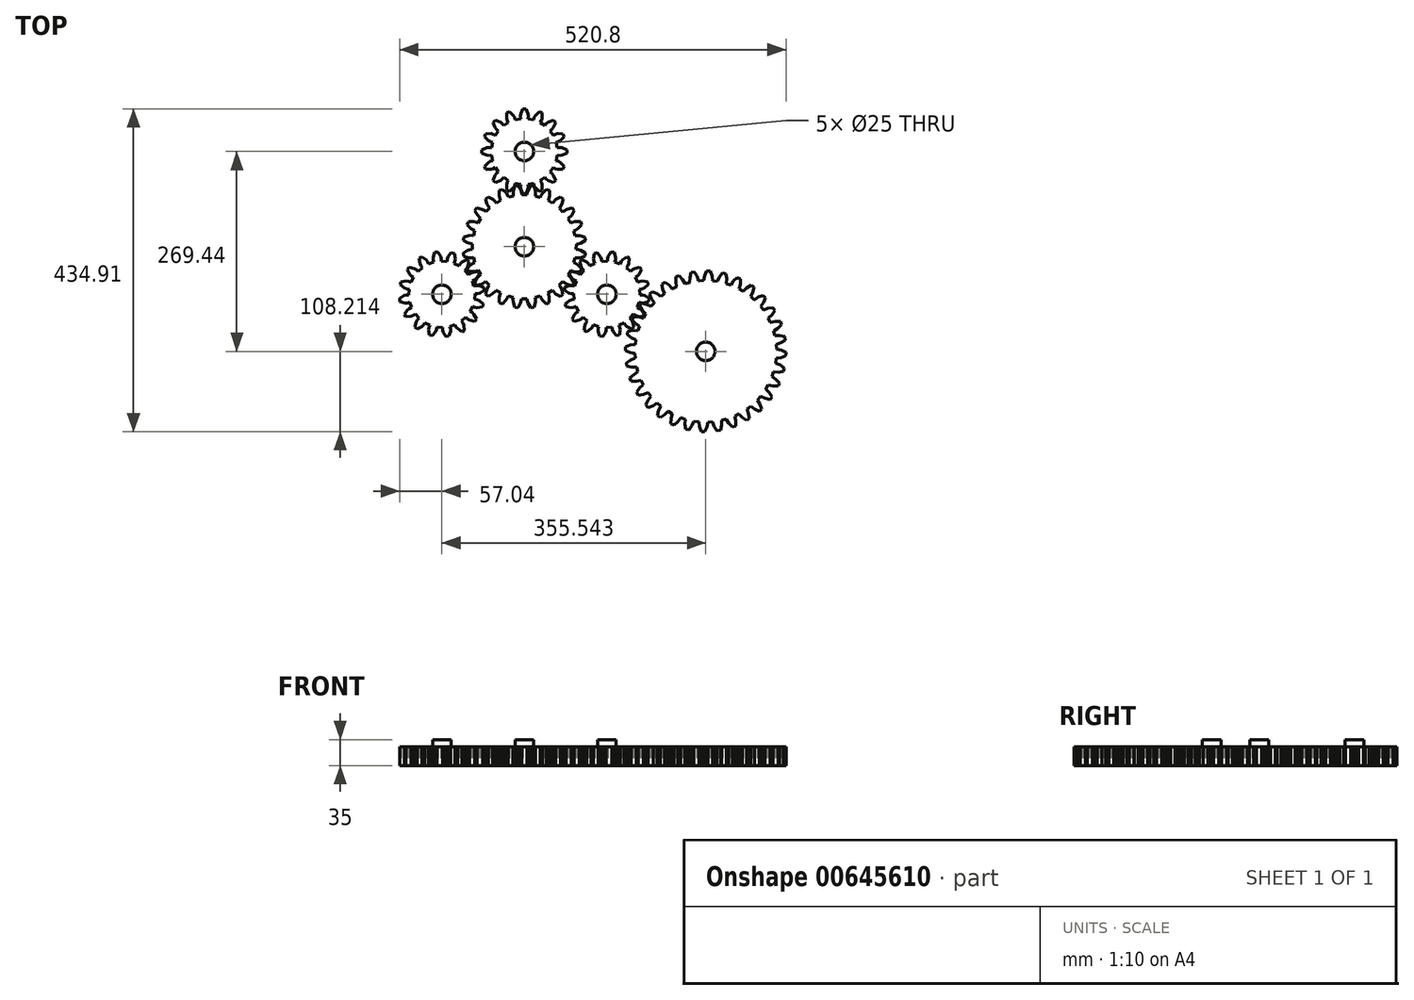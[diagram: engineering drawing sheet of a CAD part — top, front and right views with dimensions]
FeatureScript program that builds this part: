
annotation { "Feature Type Name" : "Feature", "Feature Type Description" : "" }
export const myFeature = defineFeature(function(context is Context, id is Id, definition is map)
    precondition{}
    {
        {
            var Q0;
            Q0=qCreatedBy(makeId("Top.planeOp"),FACE);
            var sketch = newSketch(context, id + "F0", { "sketchPlane" : qUnion([Q0])});
            skLineSegment(sketch, "E0", {"start": v(0, 0) * mm, "end": v(866.03, -500) * mm, "construction": true});
            skLineSegment(sketch, "E1", {"start": v(0, 0) * mm, "end": v(0, 1000) * mm, "construction": true});
            skLineSegment(sketch, "E2", {"start": v(0, 0) * mm, "end": v(-866.03, -500) * mm, "construction": true});
            skPoint(sketch, "E3.center", {"position": v(0, 0) * mm});
            skLineSegment(sketch, "E4", {"start": v(-111.14, -64.17) * mm, "end": v(0, 0) * mm});
            skLineSegment(sketch, "E5", {"start": v(0, 128.33) * mm, "end": v(0, 0) * mm});
            skLineSegment(sketch, "E6", {"start": v(0, 0) * mm, "end": v(111.14, -64.17) * mm});
            skCircle(sketch, "E7", {"center": v(0, 128.33) * mm, "radius": 12.5 * mm});
            skCircle(sketch, "E8", {"center": v(-111.14, -64.17) * mm, "radius": 12.5 * mm});
            skCircle(sketch, "E9", {"center": v(111.14, -64.17) * mm, "radius": 12.5 * mm});
            skCircle(sketch, "E10", {"center": v(0, 0) * mm, "radius": 12.5 * mm});
            skSolve(sketch);
        }
        {
            var Q0;
            Q0=qCreatedBy(makeId("Top.planeOp"),FACE);
            var sketch = newSketch(context, id + "F1", { "sketchPlane" : qUnion([Q0])});
            skLineSegment(sketch, "E11", {"start": v(66.6, -21.64) * mm, "end": v(68.28, -22.18) * mm});
            skLineSegment(sketch, "E12", {"start": v(68.28, -22.18) * mm, "end": v(72.3, -24.68) * mm});
            skLineSegment(sketch, "E13", {"start": v(72.3, -24.68) * mm, "end": v(77.25, -29.69) * mm});
            skLineSegment(sketch, "E14", {"start": v(77.25, -29.69) * mm, "end": v(75.5, -33.9) * mm});
            skLineSegment(sketch, "E15", {"start": v(75.5, -33.9) * mm, "end": v(68.46, -33.9) * mm});
            skLineSegment(sketch, "E16", {"start": v(68.46, -33.9) * mm, "end": v(63.85, -32.82) * mm});
            skLineSegment(sketch, "E17", {"start": v(63.85, -32.82) * mm, "end": v(62.28, -32.01) * mm});
            skLineSegment(sketch, "E18", {"start": v(62.28, -32.01) * mm, "end": v(58.73, -38.14) * mm});
            skLineSegment(sketch, "E19", {"start": v(58.73, -38.14) * mm, "end": v(60.2, -39.1) * mm});
            skLineSegment(sketch, "E20", {"start": v(60.2, -39.1) * mm, "end": v(63.45, -42.55) * mm});
            skLineSegment(sketch, "E21", {"start": v(63.45, -42.55) * mm, "end": v(66.94, -48.67) * mm});
            skLineSegment(sketch, "E22", {"start": v(66.94, -48.67) * mm, "end": v(64.16, -52.28) * mm});
            skLineSegment(sketch, "E23", {"start": v(64.16, -52.28) * mm, "end": v(57.35, -50.47) * mm});
            skLineSegment(sketch, "E24", {"start": v(57.35, -50.47) * mm, "end": v(53.18, -48.22) * mm});
            skLineSegment(sketch, "E25", {"start": v(53.18, -48.22) * mm, "end": v(51.87, -47.04) * mm});
            skLineSegment(sketch, "E26", {"start": v(51.87, -47.04) * mm, "end": v(46.86, -52.04) * mm});
            skLineSegment(sketch, "E27", {"start": v(46.86, -52.04) * mm, "end": v(48.04, -53.34) * mm});
            skLineSegment(sketch, "E28", {"start": v(48.04, -53.34) * mm, "end": v(50.27, -57.52) * mm});
            skLineSegment(sketch, "E29", {"start": v(50.27, -57.52) * mm, "end": v(52.06, -64.34) * mm});
            skLineSegment(sketch, "E30", {"start": v(52.06, -64.34) * mm, "end": v(48.44, -67.1) * mm});
            skLineSegment(sketch, "E31", {"start": v(48.44, -67.1) * mm, "end": v(42.33, -63.6) * mm});
            skLineSegment(sketch, "E32", {"start": v(42.33, -63.6) * mm, "end": v(38.88, -60.34) * mm});
            skLineSegment(sketch, "E33", {"start": v(38.88, -60.34) * mm, "end": v(37.93, -58.87) * mm});
            skLineSegment(sketch, "E34", {"start": v(37.93, -58.87) * mm, "end": v(31.8, -62.4) * mm});
            skLineSegment(sketch, "E35", {"start": v(31.8, -62.4) * mm, "end": v(32.6, -63.96) * mm});
            skLineSegment(sketch, "E36", {"start": v(32.6, -63.96) * mm, "end": v(33.67, -68.57) * mm});
            skLineSegment(sketch, "E37", {"start": v(33.67, -68.57) * mm, "end": v(33.63, -75.62) * mm});
            skLineSegment(sketch, "E38", {"start": v(33.63, -75.62) * mm, "end": v(29.42, -77.35) * mm});
            skLineSegment(sketch, "E39", {"start": v(29.42, -77.35) * mm, "end": v(24.43, -72.38) * mm});
            skLineSegment(sketch, "E40", {"start": v(24.43, -72.38) * mm, "end": v(21.94, -68.35) * mm});
            skLineSegment(sketch, "E41", {"start": v(21.94, -68.35) * mm, "end": v(21.4, -66.68) * mm});
            skLineSegment(sketch, "E42", {"start": v(21.4, -66.68) * mm, "end": v(14.56, -68.5) * mm});
            skLineSegment(sketch, "E43", {"start": v(14.56, -68.5) * mm, "end": v(14.93, -70.22) * mm});
            skLineSegment(sketch, "E44", {"start": v(14.93, -70.22) * mm, "end": v(14.77, -74.95) * mm});
            skLineSegment(sketch, "E45", {"start": v(14.77, -74.95) * mm, "end": v(12.91, -81.75) * mm});
            skLineSegment(sketch, "E46", {"start": v(12.91, -81.75) * mm, "end": v(8.4, -82.33) * mm});
            skLineSegment(sketch, "E47", {"start": v(8.4, -82.33) * mm, "end": v(4.86, -76.24) * mm});
            skLineSegment(sketch, "E48", {"start": v(4.86, -76.24) * mm, "end": v(3.5, -71.7) * mm});
            skLineSegment(sketch, "E49", {"start": v(3.5, -71.7) * mm, "end": v(3.42, -69.94) * mm});
            skLineSegment(sketch, "E50", {"start": v(3.42, -69.94) * mm, "end": v(-3.66, -69.93) * mm});
            skLineSegment(sketch, "E51", {"start": v(-3.66, -69.93) * mm, "end": v(-3.75, -71.69) * mm});
            skLineSegment(sketch, "E52", {"start": v(-3.75, -71.69) * mm, "end": v(-5.13, -76.22) * mm});
            skLineSegment(sketch, "E53", {"start": v(-5.13, -76.22) * mm, "end": v(-8.68, -82.3) * mm});
            skLineSegment(sketch, "E54", {"start": v(-8.68, -82.3) * mm, "end": v(-13.2, -81.7) * mm});
            skLineSegment(sketch, "E55", {"start": v(-13.2, -81.7) * mm, "end": v(-15.03, -74.9) * mm});
            skLineSegment(sketch, "E56", {"start": v(-15.03, -74.9) * mm, "end": v(-15.18, -70.16) * mm});
            skLineSegment(sketch, "E57", {"start": v(-15.18, -70.16) * mm, "end": v(-14.8, -68.45) * mm});
            skLineSegment(sketch, "E58", {"start": v(-14.8, -68.45) * mm, "end": v(-21.64, -66.6) * mm});
            skLineSegment(sketch, "E59", {"start": v(-21.64, -66.6) * mm, "end": v(-22.18, -68.28) * mm});
            skLineSegment(sketch, "E60", {"start": v(-22.18, -68.28) * mm, "end": v(-24.68, -72.3) * mm});
            skLineSegment(sketch, "E61", {"start": v(-24.68, -72.3) * mm, "end": v(-29.69, -77.25) * mm});
            skLineSegment(sketch, "E62", {"start": v(-29.69, -77.25) * mm, "end": v(-33.9, -75.5) * mm});
            skLineSegment(sketch, "E63", {"start": v(-33.9, -75.5) * mm, "end": v(-33.9, -68.46) * mm});
            skLineSegment(sketch, "E64", {"start": v(-33.9, -68.46) * mm, "end": v(-32.82, -63.85) * mm});
            skLineSegment(sketch, "E65", {"start": v(-32.82, -63.85) * mm, "end": v(-32.01, -62.28) * mm});
            skLineSegment(sketch, "E66", {"start": v(-32.01, -62.28) * mm, "end": v(-38.14, -58.73) * mm});
            skLineSegment(sketch, "E67", {"start": v(-38.14, -58.73) * mm, "end": v(-39.1, -60.2) * mm});
            skLineSegment(sketch, "E68", {"start": v(-39.1, -60.2) * mm, "end": v(-42.55, -63.45) * mm});
            skLineSegment(sketch, "E69", {"start": v(-42.55, -63.45) * mm, "end": v(-48.67, -66.94) * mm});
            skLineSegment(sketch, "E70", {"start": v(-48.67, -66.94) * mm, "end": v(-52.28, -64.16) * mm});
            skLineSegment(sketch, "E71", {"start": v(-52.28, -64.16) * mm, "end": v(-50.47, -57.35) * mm});
            skLineSegment(sketch, "E72", {"start": v(-50.47, -57.35) * mm, "end": v(-48.22, -53.18) * mm});
            skLineSegment(sketch, "E73", {"start": v(-48.22, -53.18) * mm, "end": v(-47.04, -51.87) * mm});
            skLineSegment(sketch, "E74", {"start": v(-47.04, -51.87) * mm, "end": v(-52.04, -46.86) * mm});
            skLineSegment(sketch, "E75", {"start": v(-52.04, -46.86) * mm, "end": v(-53.34, -48.04) * mm});
            skLineSegment(sketch, "E76", {"start": v(-53.34, -48.04) * mm, "end": v(-57.52, -50.27) * mm});
            skLineSegment(sketch, "E77", {"start": v(-57.52, -50.27) * mm, "end": v(-64.34, -52.06) * mm});
            skLineSegment(sketch, "E78", {"start": v(-64.34, -52.06) * mm, "end": v(-67.1, -48.44) * mm});
            skLineSegment(sketch, "E79", {"start": v(-67.1, -48.44) * mm, "end": v(-63.6, -42.33) * mm});
            skLineSegment(sketch, "E80", {"start": v(-63.6, -42.33) * mm, "end": v(-60.34, -38.88) * mm});
            skLineSegment(sketch, "E81", {"start": v(-60.34, -38.88) * mm, "end": v(-58.87, -37.93) * mm});
            skLineSegment(sketch, "E82", {"start": v(-58.87, -37.93) * mm, "end": v(-62.4, -31.8) * mm});
            skLineSegment(sketch, "E83", {"start": v(-62.4, -31.8) * mm, "end": v(-63.96, -32.6) * mm});
            skLineSegment(sketch, "E84", {"start": v(-63.96, -32.6) * mm, "end": v(-68.57, -33.67) * mm});
            skLineSegment(sketch, "E85", {"start": v(-68.57, -33.67) * mm, "end": v(-75.62, -33.63) * mm});
            skLineSegment(sketch, "E86", {"start": v(-75.62, -33.63) * mm, "end": v(-77.35, -29.42) * mm});
            skLineSegment(sketch, "E87", {"start": v(-77.35, -29.42) * mm, "end": v(-72.38, -24.43) * mm});
            skLineSegment(sketch, "E88", {"start": v(-72.38, -24.43) * mm, "end": v(-68.35, -21.94) * mm});
            skLineSegment(sketch, "E89", {"start": v(-68.35, -21.94) * mm, "end": v(-66.68, -21.4) * mm});
            skLineSegment(sketch, "E90", {"start": v(-66.68, -21.4) * mm, "end": v(-68.5, -14.56) * mm});
            skLineSegment(sketch, "E91", {"start": v(-68.5, -14.56) * mm, "end": v(-70.22, -14.93) * mm});
            skLineSegment(sketch, "E92", {"start": v(-70.22, -14.93) * mm, "end": v(-74.95, -14.77) * mm});
            skLineSegment(sketch, "E93", {"start": v(-74.95, -14.77) * mm, "end": v(-81.75, -12.91) * mm});
            skLineSegment(sketch, "E94", {"start": v(-81.75, -12.91) * mm, "end": v(-82.33, -8.4) * mm});
            skLineSegment(sketch, "E95", {"start": v(-82.33, -8.4) * mm, "end": v(-76.24, -4.86) * mm});
            skLineSegment(sketch, "E96", {"start": v(-76.24, -4.86) * mm, "end": v(-71.7, -3.5) * mm});
            skLineSegment(sketch, "E97", {"start": v(-71.7, -3.5) * mm, "end": v(-69.94, -3.42) * mm});
            skLineSegment(sketch, "E98", {"start": v(-69.94, -3.42) * mm, "end": v(-69.93, 3.66) * mm});
            skLineSegment(sketch, "E99", {"start": v(-69.93, 3.66) * mm, "end": v(-71.69, 3.75) * mm});
            skLineSegment(sketch, "E100", {"start": v(-71.69, 3.75) * mm, "end": v(-76.22, 5.13) * mm});
            skLineSegment(sketch, "E101", {"start": v(-76.22, 5.13) * mm, "end": v(-82.3, 8.68) * mm});
            skLineSegment(sketch, "E102", {"start": v(-82.3, 8.68) * mm, "end": v(-81.7, 13.2) * mm});
            skLineSegment(sketch, "E103", {"start": v(-81.7, 13.2) * mm, "end": v(-74.9, 15.03) * mm});
            skLineSegment(sketch, "E104", {"start": v(-74.9, 15.03) * mm, "end": v(-70.16, 15.18) * mm});
            skLineSegment(sketch, "E105", {"start": v(-70.16, 15.18) * mm, "end": v(-68.45, 14.8) * mm});
            skLineSegment(sketch, "E106", {"start": v(-68.45, 14.8) * mm, "end": v(-66.6, 21.64) * mm});
            skLineSegment(sketch, "E107", {"start": v(-66.6, 21.64) * mm, "end": v(-68.28, 22.18) * mm});
            skLineSegment(sketch, "E108", {"start": v(-68.28, 22.18) * mm, "end": v(-72.3, 24.68) * mm});
            skLineSegment(sketch, "E109", {"start": v(-72.3, 24.68) * mm, "end": v(-77.25, 29.69) * mm});
            skLineSegment(sketch, "E110", {"start": v(-77.25, 29.69) * mm, "end": v(-75.5, 33.9) * mm});
            skLineSegment(sketch, "E111", {"start": v(-75.5, 33.9) * mm, "end": v(-68.46, 33.9) * mm});
            skLineSegment(sketch, "E112", {"start": v(-68.46, 33.9) * mm, "end": v(-63.85, 32.82) * mm});
            skLineSegment(sketch, "E113", {"start": v(-63.85, 32.82) * mm, "end": v(-62.28, 32.01) * mm});
            skLineSegment(sketch, "E114", {"start": v(-62.28, 32.01) * mm, "end": v(-58.73, 38.14) * mm});
            skLineSegment(sketch, "E115", {"start": v(-58.73, 38.14) * mm, "end": v(-60.2, 39.1) * mm});
            skLineSegment(sketch, "E116", {"start": v(-60.2, 39.1) * mm, "end": v(-63.45, 42.55) * mm});
            skLineSegment(sketch, "E117", {"start": v(-63.45, 42.55) * mm, "end": v(-66.94, 48.67) * mm});
            skLineSegment(sketch, "E118", {"start": v(-66.94, 48.67) * mm, "end": v(-64.16, 52.28) * mm});
            skLineSegment(sketch, "E119", {"start": v(-64.16, 52.28) * mm, "end": v(-57.35, 50.47) * mm});
            skLineSegment(sketch, "E120", {"start": v(-57.35, 50.47) * mm, "end": v(-53.18, 48.22) * mm});
            skLineSegment(sketch, "E121", {"start": v(-53.18, 48.22) * mm, "end": v(-51.87, 47.04) * mm});
            skLineSegment(sketch, "E122", {"start": v(-51.87, 47.04) * mm, "end": v(-46.86, 52.04) * mm});
            skLineSegment(sketch, "E123", {"start": v(-46.86, 52.04) * mm, "end": v(-48.04, 53.34) * mm});
            skLineSegment(sketch, "E124", {"start": v(-48.04, 53.34) * mm, "end": v(-50.27, 57.52) * mm});
            skLineSegment(sketch, "E125", {"start": v(-50.27, 57.52) * mm, "end": v(-52.06, 64.34) * mm});
            skLineSegment(sketch, "E126", {"start": v(-52.06, 64.34) * mm, "end": v(-48.44, 67.1) * mm});
            skLineSegment(sketch, "E127", {"start": v(-48.44, 67.1) * mm, "end": v(-42.33, 63.6) * mm});
            skLineSegment(sketch, "E128", {"start": v(-42.33, 63.6) * mm, "end": v(-38.88, 60.34) * mm});
            skLineSegment(sketch, "E129", {"start": v(-38.88, 60.34) * mm, "end": v(-37.93, 58.87) * mm});
            skLineSegment(sketch, "E130", {"start": v(-37.93, 58.87) * mm, "end": v(-31.8, 62.4) * mm});
            skLineSegment(sketch, "E131", {"start": v(-31.8, 62.4) * mm, "end": v(-32.6, 63.96) * mm});
            skLineSegment(sketch, "E132", {"start": v(-32.6, 63.96) * mm, "end": v(-33.67, 68.57) * mm});
            skLineSegment(sketch, "E133", {"start": v(-33.67, 68.57) * mm, "end": v(-33.63, 75.62) * mm});
            skLineSegment(sketch, "E134", {"start": v(-33.63, 75.62) * mm, "end": v(-29.42, 77.35) * mm});
            skLineSegment(sketch, "E135", {"start": v(-29.42, 77.35) * mm, "end": v(-24.43, 72.38) * mm});
            skLineSegment(sketch, "E136", {"start": v(-24.43, 72.38) * mm, "end": v(-21.94, 68.35) * mm});
            skLineSegment(sketch, "E137", {"start": v(-21.94, 68.35) * mm, "end": v(-21.4, 66.68) * mm});
            skLineSegment(sketch, "E138", {"start": v(-21.4, 66.68) * mm, "end": v(-14.56, 68.5) * mm});
            skLineSegment(sketch, "E139", {"start": v(-14.56, 68.5) * mm, "end": v(-14.93, 70.22) * mm});
            skLineSegment(sketch, "E140", {"start": v(-14.93, 70.22) * mm, "end": v(-14.77, 74.95) * mm});
            skLineSegment(sketch, "E141", {"start": v(-14.77, 74.95) * mm, "end": v(-12.91, 81.75) * mm});
            skLineSegment(sketch, "E142", {"start": v(-12.91, 81.75) * mm, "end": v(-8.4, 82.33) * mm});
            skLineSegment(sketch, "E143", {"start": v(-8.4, 82.33) * mm, "end": v(-4.86, 76.24) * mm});
            skLineSegment(sketch, "E144", {"start": v(-4.86, 76.24) * mm, "end": v(-3.5, 71.7) * mm});
            skLineSegment(sketch, "E145", {"start": v(-3.5, 71.7) * mm, "end": v(-3.42, 69.94) * mm});
            skLineSegment(sketch, "E146", {"start": v(-3.42, 69.94) * mm, "end": v(3.66, 69.93) * mm});
            skLineSegment(sketch, "E147", {"start": v(3.66, 69.93) * mm, "end": v(3.75, 71.69) * mm});
            skLineSegment(sketch, "E148", {"start": v(3.75, 71.69) * mm, "end": v(5.13, 76.22) * mm});
            skLineSegment(sketch, "E149", {"start": v(5.13, 76.22) * mm, "end": v(8.68, 82.3) * mm});
            skLineSegment(sketch, "E150", {"start": v(8.68, 82.3) * mm, "end": v(13.2, 81.7) * mm});
            skLineSegment(sketch, "E151", {"start": v(13.2, 81.7) * mm, "end": v(15.03, 74.9) * mm});
            skLineSegment(sketch, "E152", {"start": v(15.03, 74.9) * mm, "end": v(15.18, 70.16) * mm});
            skLineSegment(sketch, "E153", {"start": v(15.18, 70.16) * mm, "end": v(14.8, 68.45) * mm});
            skLineSegment(sketch, "E154", {"start": v(14.8, 68.45) * mm, "end": v(21.64, 66.6) * mm});
            skLineSegment(sketch, "E155", {"start": v(21.64, 66.6) * mm, "end": v(22.18, 68.28) * mm});
            skLineSegment(sketch, "E156", {"start": v(22.18, 68.28) * mm, "end": v(24.68, 72.3) * mm});
            skLineSegment(sketch, "E157", {"start": v(24.68, 72.3) * mm, "end": v(29.69, 77.25) * mm});
            skLineSegment(sketch, "E158", {"start": v(29.69, 77.25) * mm, "end": v(33.9, 75.5) * mm});
            skLineSegment(sketch, "E159", {"start": v(33.9, 75.5) * mm, "end": v(33.9, 68.46) * mm});
            skLineSegment(sketch, "E160", {"start": v(33.9, 68.46) * mm, "end": v(32.82, 63.85) * mm});
            skLineSegment(sketch, "E161", {"start": v(32.82, 63.85) * mm, "end": v(32.01, 62.28) * mm});
            skLineSegment(sketch, "E162", {"start": v(32.01, 62.28) * mm, "end": v(38.14, 58.73) * mm});
            skLineSegment(sketch, "E163", {"start": v(38.14, 58.73) * mm, "end": v(39.1, 60.2) * mm});
            skLineSegment(sketch, "E164", {"start": v(39.1, 60.2) * mm, "end": v(42.55, 63.45) * mm});
            skLineSegment(sketch, "E165", {"start": v(42.55, 63.45) * mm, "end": v(48.67, 66.94) * mm});
            skLineSegment(sketch, "E166", {"start": v(48.67, 66.94) * mm, "end": v(52.28, 64.16) * mm});
            skLineSegment(sketch, "E167", {"start": v(52.28, 64.16) * mm, "end": v(50.47, 57.35) * mm});
            skLineSegment(sketch, "E168", {"start": v(50.47, 57.35) * mm, "end": v(48.22, 53.18) * mm});
            skLineSegment(sketch, "E169", {"start": v(48.22, 53.18) * mm, "end": v(47.04, 51.87) * mm});
            skLineSegment(sketch, "E170", {"start": v(47.04, 51.87) * mm, "end": v(52.04, 46.86) * mm});
            skLineSegment(sketch, "E171", {"start": v(52.04, 46.86) * mm, "end": v(53.34, 48.04) * mm});
            skLineSegment(sketch, "E172", {"start": v(53.34, 48.04) * mm, "end": v(57.52, 50.27) * mm});
            skLineSegment(sketch, "E173", {"start": v(57.52, 50.27) * mm, "end": v(64.34, 52.06) * mm});
            skLineSegment(sketch, "E174", {"start": v(64.34, 52.06) * mm, "end": v(67.1, 48.44) * mm});
            skLineSegment(sketch, "E175", {"start": v(67.1, 48.44) * mm, "end": v(63.6, 42.33) * mm});
            skLineSegment(sketch, "E176", {"start": v(63.6, 42.33) * mm, "end": v(60.34, 38.88) * mm});
            skLineSegment(sketch, "E177", {"start": v(60.34, 38.88) * mm, "end": v(58.87, 37.93) * mm});
            skLineSegment(sketch, "E178", {"start": v(58.87, 37.93) * mm, "end": v(62.4, 31.8) * mm});
            skLineSegment(sketch, "E179", {"start": v(62.4, 31.8) * mm, "end": v(63.96, 32.6) * mm});
            skLineSegment(sketch, "E180", {"start": v(63.96, 32.6) * mm, "end": v(68.57, 33.67) * mm});
            skLineSegment(sketch, "E181", {"start": v(68.57, 33.67) * mm, "end": v(75.62, 33.63) * mm});
            skLineSegment(sketch, "E182", {"start": v(75.62, 33.63) * mm, "end": v(77.35, 29.42) * mm});
            skLineSegment(sketch, "E183", {"start": v(77.35, 29.42) * mm, "end": v(72.38, 24.43) * mm});
            skLineSegment(sketch, "E184", {"start": v(72.38, 24.43) * mm, "end": v(68.35, 21.94) * mm});
            skLineSegment(sketch, "E185", {"start": v(68.35, 21.94) * mm, "end": v(66.68, 21.4) * mm});
            skLineSegment(sketch, "E186", {"start": v(66.68, 21.4) * mm, "end": v(68.5, 14.56) * mm});
            skLineSegment(sketch, "E187", {"start": v(68.5, 14.56) * mm, "end": v(70.22, 14.93) * mm});
            skLineSegment(sketch, "E188", {"start": v(70.22, 14.93) * mm, "end": v(74.95, 14.77) * mm});
            skLineSegment(sketch, "E189", {"start": v(74.95, 14.77) * mm, "end": v(81.75, 12.91) * mm});
            skLineSegment(sketch, "E190", {"start": v(81.75, 12.91) * mm, "end": v(82.33, 8.4) * mm});
            skLineSegment(sketch, "E191", {"start": v(82.33, 8.4) * mm, "end": v(76.24, 4.86) * mm});
            skLineSegment(sketch, "E192", {"start": v(76.24, 4.86) * mm, "end": v(71.7, 3.5) * mm});
            skLineSegment(sketch, "E193", {"start": v(71.7, 3.5) * mm, "end": v(69.94, 3.42) * mm});
            skLineSegment(sketch, "E194", {"start": v(69.94, 3.42) * mm, "end": v(69.93, -3.66) * mm});
            skLineSegment(sketch, "E195", {"start": v(69.93, -3.66) * mm, "end": v(71.69, -3.75) * mm});
            skLineSegment(sketch, "E196", {"start": v(71.69, -3.75) * mm, "end": v(76.22, -5.13) * mm});
            skLineSegment(sketch, "E197", {"start": v(76.22, -5.13) * mm, "end": v(82.3, -8.68) * mm});
            skLineSegment(sketch, "E198", {"start": v(82.3, -8.68) * mm, "end": v(81.7, -13.2) * mm});
            skLineSegment(sketch, "E199", {"start": v(81.7, -13.2) * mm, "end": v(74.9, -15.03) * mm});
            skLineSegment(sketch, "E200", {"start": v(74.9, -15.03) * mm, "end": v(70.16, -15.18) * mm});
            skLineSegment(sketch, "E201", {"start": v(70.16, -15.18) * mm, "end": v(68.45, -14.8) * mm});
            skLineSegment(sketch, "E202", {"start": v(68.45, -14.8) * mm, "end": v(66.6, -21.64) * mm});
            skCircle(sketch, "E203", {"center": v(0, 0) * mm, "radius": 12.5 * mm});
            skSolve(sketch);
        }
        {
            var Q0;
            Q0=qCreatedBy(makeId("Top.planeOp"),FACE);
            var sketch = newSketch(context, id + "F2", { "sketchPlane" : qUnion([Q0])});
            skLineSegment(sketch, "E204", {"start": v(155.7, -64.96) * mm, "end": v(159, -65.02) * mm});
            skLineSegment(sketch, "E205", {"start": v(159, -65.02) * mm, "end": v(162.04, -65.83) * mm});
            skLineSegment(sketch, "E206", {"start": v(162.04, -65.83) * mm, "end": v(168.18, -69.54) * mm});
            skLineSegment(sketch, "E207", {"start": v(168.18, -69.54) * mm, "end": v(167.63, -73.74) * mm});
            skLineSegment(sketch, "E208", {"start": v(167.63, -73.74) * mm, "end": v(160.74, -75.73) * mm});
            skLineSegment(sketch, "E209", {"start": v(160.74, -75.73) * mm, "end": v(157.58, -75.73) * mm});
            skLineSegment(sketch, "E210", {"start": v(157.58, -75.73) * mm, "end": v(154.38, -74.93) * mm});
            skLineSegment(sketch, "E211", {"start": v(154.38, -74.93) * mm, "end": v(152, -81.95) * mm});
            skLineSegment(sketch, "E212", {"start": v(152, -81.95) * mm, "end": v(155.02, -83.27) * mm});
            skLineSegment(sketch, "E213", {"start": v(155.02, -83.27) * mm, "end": v(157.53, -85.19) * mm});
            skLineSegment(sketch, "E214", {"start": v(157.53, -85.19) * mm, "end": v(161.79, -90.96) * mm});
            skLineSegment(sketch, "E215", {"start": v(161.79, -90.96) * mm, "end": v(159.67, -94.63) * mm});
            skLineSegment(sketch, "E216", {"start": v(159.67, -94.63) * mm, "end": v(152.54, -93.83) * mm});
            skLineSegment(sketch, "E217", {"start": v(152.54, -93.83) * mm, "end": v(149.62, -92.62) * mm});
            skLineSegment(sketch, "E218", {"start": v(149.62, -92.62) * mm, "end": v(146.97, -90.66) * mm});
            skLineSegment(sketch, "E219", {"start": v(146.97, -90.66) * mm, "end": v(142.08, -96.23) * mm});
            skLineSegment(sketch, "E220", {"start": v(142.08, -96.23) * mm, "end": v(144.37, -98.6) * mm});
            skLineSegment(sketch, "E221", {"start": v(144.37, -98.6) * mm, "end": v(145.96, -101.34) * mm});
            skLineSegment(sketch, "E222", {"start": v(145.96, -101.34) * mm, "end": v(147.68, -108.3) * mm});
            skLineSegment(sketch, "E223", {"start": v(147.68, -108.3) * mm, "end": v(144.32, -110.88) * mm});
            skLineSegment(sketch, "E224", {"start": v(144.32, -110.88) * mm, "end": v(138.03, -107.42) * mm});
            skLineSegment(sketch, "E225", {"start": v(138.03, -107.42) * mm, "end": v(135.8, -105.18) * mm});
            skLineSegment(sketch, "E226", {"start": v(135.8, -105.18) * mm, "end": v(134.1, -102.36) * mm});
            skLineSegment(sketch, "E227", {"start": v(134.1, -102.36) * mm, "end": v(127.46, -105.64) * mm});
            skLineSegment(sketch, "E228", {"start": v(127.46, -105.64) * mm, "end": v(128.66, -108.7) * mm});
            skLineSegment(sketch, "E229", {"start": v(128.66, -108.7) * mm, "end": v(129.08, -111.83) * mm});
            skLineSegment(sketch, "E230", {"start": v(129.08, -111.83) * mm, "end": v(128, -118.92) * mm});
            skLineSegment(sketch, "E231", {"start": v(128, -118.92) * mm, "end": v(123.91, -120.02) * mm});
            skLineSegment(sketch, "E232", {"start": v(123.91, -120.02) * mm, "end": v(119.44, -114.42) * mm});
            skLineSegment(sketch, "E233", {"start": v(119.44, -114.42) * mm, "end": v(118.23, -111.5) * mm});
            skLineSegment(sketch, "E234", {"start": v(118.23, -111.5) * mm, "end": v(117.74, -108.24) * mm});
            skLineSegment(sketch, "E235", {"start": v(117.74, -108.24) * mm, "end": v(110.35, -108.72) * mm});
            skLineSegment(sketch, "E236", {"start": v(110.35, -108.72) * mm, "end": v(110.29, -112.02) * mm});
            skLineSegment(sketch, "E237", {"start": v(110.29, -112.02) * mm, "end": v(109.47, -115.07) * mm});
            skLineSegment(sketch, "E238", {"start": v(109.47, -115.07) * mm, "end": v(105.77, -121.21) * mm});
            skLineSegment(sketch, "E239", {"start": v(105.77, -121.21) * mm, "end": v(101.57, -120.66) * mm});
            skLineSegment(sketch, "E240", {"start": v(101.57, -120.66) * mm, "end": v(99.58, -113.77) * mm});
            skLineSegment(sketch, "E241", {"start": v(99.58, -113.77) * mm, "end": v(99.58, -110.6) * mm});
            skLineSegment(sketch, "E242", {"start": v(99.58, -110.6) * mm, "end": v(100.38, -107.41) * mm});
            skLineSegment(sketch, "E243", {"start": v(100.38, -107.41) * mm, "end": v(93.36, -105.03) * mm});
            skLineSegment(sketch, "E244", {"start": v(93.36, -105.03) * mm, "end": v(92.04, -108.05) * mm});
            skLineSegment(sketch, "E245", {"start": v(92.04, -108.05) * mm, "end": v(90.12, -110.56) * mm});
            skLineSegment(sketch, "E246", {"start": v(90.12, -110.56) * mm, "end": v(84.35, -114.81) * mm});
            skLineSegment(sketch, "E247", {"start": v(84.35, -114.81) * mm, "end": v(80.68, -112.7) * mm});
            skLineSegment(sketch, "E248", {"start": v(80.68, -112.7) * mm, "end": v(81.48, -105.56) * mm});
            skLineSegment(sketch, "E249", {"start": v(81.48, -105.56) * mm, "end": v(82.69, -102.65) * mm});
            skLineSegment(sketch, "E250", {"start": v(82.69, -102.65) * mm, "end": v(84.65, -100) * mm});
            skLineSegment(sketch, "E251", {"start": v(84.65, -100) * mm, "end": v(79.07, -95.11) * mm});
            skLineSegment(sketch, "E252", {"start": v(79.07, -95.11) * mm, "end": v(76.7, -97.4) * mm});
            skLineSegment(sketch, "E253", {"start": v(76.7, -97.4) * mm, "end": v(73.97, -98.98) * mm});
            skLineSegment(sketch, "E254", {"start": v(73.97, -98.98) * mm, "end": v(67, -100.7) * mm});
            skLineSegment(sketch, "E255", {"start": v(67, -100.7) * mm, "end": v(64.43, -97.34) * mm});
            skLineSegment(sketch, "E256", {"start": v(64.43, -97.34) * mm, "end": v(67.9, -91.06) * mm});
            skLineSegment(sketch, "E257", {"start": v(67.9, -91.06) * mm, "end": v(70.13, -88.83) * mm});
            skLineSegment(sketch, "E258", {"start": v(70.13, -88.83) * mm, "end": v(72.95, -87.13) * mm});
            skLineSegment(sketch, "E259", {"start": v(72.95, -87.13) * mm, "end": v(69.67, -80.48) * mm});
            skLineSegment(sketch, "E260", {"start": v(69.67, -80.48) * mm, "end": v(66.6, -81.7) * mm});
            skLineSegment(sketch, "E261", {"start": v(66.6, -81.7) * mm, "end": v(63.48, -82.1) * mm});
            skLineSegment(sketch, "E262", {"start": v(63.48, -82.1) * mm, "end": v(56.38, -81.03) * mm});
            skLineSegment(sketch, "E263", {"start": v(56.38, -81.03) * mm, "end": v(55.29, -76.94) * mm});
            skLineSegment(sketch, "E264", {"start": v(55.29, -76.94) * mm, "end": v(60.9, -72.46) * mm});
            skLineSegment(sketch, "E265", {"start": v(60.9, -72.46) * mm, "end": v(63.81, -71.26) * mm});
            skLineSegment(sketch, "E266", {"start": v(63.81, -71.26) * mm, "end": v(67.07, -70.77) * mm});
            skLineSegment(sketch, "E267", {"start": v(67.07, -70.77) * mm, "end": v(66.58, -63.37) * mm});
            skLineSegment(sketch, "E268", {"start": v(66.58, -63.37) * mm, "end": v(63.29, -63.31) * mm});
            skLineSegment(sketch, "E269", {"start": v(63.29, -63.31) * mm, "end": v(60.24, -62.5) * mm});
            skLineSegment(sketch, "E270", {"start": v(60.24, -62.5) * mm, "end": v(54.1, -58.8) * mm});
            skLineSegment(sketch, "E271", {"start": v(54.1, -58.8) * mm, "end": v(54.65, -54.6) * mm});
            skLineSegment(sketch, "E272", {"start": v(54.65, -54.6) * mm, "end": v(61.54, -52.6) * mm});
            skLineSegment(sketch, "E273", {"start": v(61.54, -52.6) * mm, "end": v(64.7, -52.6) * mm});
            skLineSegment(sketch, "E274", {"start": v(64.7, -52.6) * mm, "end": v(67.9, -53.4) * mm});
            skLineSegment(sketch, "E275", {"start": v(67.9, -53.4) * mm, "end": v(70.28, -46.38) * mm});
            skLineSegment(sketch, "E276", {"start": v(70.28, -46.38) * mm, "end": v(67.26, -45.07) * mm});
            skLineSegment(sketch, "E277", {"start": v(67.26, -45.07) * mm, "end": v(64.75, -43.15) * mm});
            skLineSegment(sketch, "E278", {"start": v(64.75, -43.15) * mm, "end": v(60.5, -37.37) * mm});
            skLineSegment(sketch, "E279", {"start": v(60.5, -37.37) * mm, "end": v(62.61, -33.7) * mm});
            skLineSegment(sketch, "E280", {"start": v(62.61, -33.7) * mm, "end": v(69.74, -34.5) * mm});
            skLineSegment(sketch, "E281", {"start": v(69.74, -34.5) * mm, "end": v(72.66, -35.71) * mm});
            skLineSegment(sketch, "E282", {"start": v(72.66, -35.71) * mm, "end": v(75.3, -37.67) * mm});
            skLineSegment(sketch, "E283", {"start": v(75.3, -37.67) * mm, "end": v(80.2, -32.1) * mm});
            skLineSegment(sketch, "E284", {"start": v(80.2, -32.1) * mm, "end": v(77.9, -29.73) * mm});
            skLineSegment(sketch, "E285", {"start": v(77.9, -29.73) * mm, "end": v(76.33, -27) * mm});
            skLineSegment(sketch, "E286", {"start": v(76.33, -27) * mm, "end": v(74.6, -20.03) * mm});
            skLineSegment(sketch, "E287", {"start": v(74.6, -20.03) * mm, "end": v(77.97, -17.45) * mm});
            skLineSegment(sketch, "E288", {"start": v(77.97, -17.45) * mm, "end": v(84.25, -20.92) * mm});
            skLineSegment(sketch, "E289", {"start": v(84.25, -20.92) * mm, "end": v(86.48, -23.15) * mm});
            skLineSegment(sketch, "E290", {"start": v(86.48, -23.15) * mm, "end": v(88.17, -25.98) * mm});
            skLineSegment(sketch, "E291", {"start": v(88.17, -25.98) * mm, "end": v(94.82, -22.7) * mm});
            skLineSegment(sketch, "E292", {"start": v(94.82, -22.7) * mm, "end": v(93.62, -19.63) * mm});
            skLineSegment(sketch, "E293", {"start": v(93.62, -19.63) * mm, "end": v(93.2, -16.5) * mm});
            skLineSegment(sketch, "E294", {"start": v(93.2, -16.5) * mm, "end": v(94.27, -9.4) * mm});
            skLineSegment(sketch, "E295", {"start": v(94.27, -9.4) * mm, "end": v(98.37, -8.31) * mm});
            skLineSegment(sketch, "E296", {"start": v(98.37, -8.31) * mm, "end": v(102.84, -13.92) * mm});
            skLineSegment(sketch, "E297", {"start": v(102.84, -13.92) * mm, "end": v(104.05, -16.84) * mm});
            skLineSegment(sketch, "E298", {"start": v(104.05, -16.84) * mm, "end": v(104.54, -20.1) * mm});
            skLineSegment(sketch, "E299", {"start": v(104.54, -20.1) * mm, "end": v(111.93, -19.61) * mm});
            skLineSegment(sketch, "E300", {"start": v(111.93, -19.61) * mm, "end": v(112, -16.32) * mm});
            skLineSegment(sketch, "E301", {"start": v(112, -16.32) * mm, "end": v(112.8, -13.26) * mm});
            skLineSegment(sketch, "E302", {"start": v(112.8, -13.26) * mm, "end": v(116.51, -7.12) * mm});
            skLineSegment(sketch, "E303", {"start": v(116.51, -7.12) * mm, "end": v(120.71, -7.68) * mm});
            skLineSegment(sketch, "E304", {"start": v(120.71, -7.68) * mm, "end": v(122.7, -14.57) * mm});
            skLineSegment(sketch, "E305", {"start": v(122.7, -14.57) * mm, "end": v(122.7, -17.73) * mm});
            skLineSegment(sketch, "E306", {"start": v(122.7, -17.73) * mm, "end": v(121.9, -20.92) * mm});
            skLineSegment(sketch, "E307", {"start": v(121.9, -20.92) * mm, "end": v(128.92, -23.3) * mm});
            skLineSegment(sketch, "E308", {"start": v(128.92, -23.3) * mm, "end": v(130.24, -20.29) * mm});
            skLineSegment(sketch, "E309", {"start": v(130.24, -20.29) * mm, "end": v(132.16, -17.78) * mm});
            skLineSegment(sketch, "E310", {"start": v(132.16, -17.78) * mm, "end": v(137.93, -13.52) * mm});
            skLineSegment(sketch, "E311", {"start": v(137.93, -13.52) * mm, "end": v(141.6, -15.64) * mm});
            skLineSegment(sketch, "E312", {"start": v(141.6, -15.64) * mm, "end": v(140.8, -22.77) * mm});
            skLineSegment(sketch, "E313", {"start": v(140.8, -22.77) * mm, "end": v(139.6, -25.69) * mm});
            skLineSegment(sketch, "E314", {"start": v(139.6, -25.69) * mm, "end": v(137.63, -28.33) * mm});
            skLineSegment(sketch, "E315", {"start": v(137.63, -28.33) * mm, "end": v(143.2, -33.22) * mm});
            skLineSegment(sketch, "E316", {"start": v(143.2, -33.22) * mm, "end": v(145.58, -30.93) * mm});
            skLineSegment(sketch, "E317", {"start": v(145.58, -30.93) * mm, "end": v(148.31, -29.35) * mm});
            skLineSegment(sketch, "E318", {"start": v(148.31, -29.35) * mm, "end": v(155.28, -27.63) * mm});
            skLineSegment(sketch, "E319", {"start": v(155.28, -27.63) * mm, "end": v(157.85, -31) * mm});
            skLineSegment(sketch, "E320", {"start": v(157.85, -31) * mm, "end": v(154.39, -37.27) * mm});
            skLineSegment(sketch, "E321", {"start": v(154.39, -37.27) * mm, "end": v(152.15, -39.5) * mm});
            skLineSegment(sketch, "E322", {"start": v(152.15, -39.5) * mm, "end": v(149.33, -41.2) * mm});
            skLineSegment(sketch, "E323", {"start": v(149.33, -41.2) * mm, "end": v(152.6, -47.85) * mm});
            skLineSegment(sketch, "E324", {"start": v(152.6, -47.85) * mm, "end": v(155.67, -46.64) * mm});
            skLineSegment(sketch, "E325", {"start": v(155.67, -46.64) * mm, "end": v(158.8, -46.23) * mm});
            skLineSegment(sketch, "E326", {"start": v(158.8, -46.23) * mm, "end": v(165.9, -47.3) * mm});
            skLineSegment(sketch, "E327", {"start": v(165.9, -47.3) * mm, "end": v(167, -51.4) * mm});
            skLineSegment(sketch, "E328", {"start": v(167, -51.4) * mm, "end": v(161.39, -55.87) * mm});
            skLineSegment(sketch, "E329", {"start": v(161.39, -55.87) * mm, "end": v(158.47, -57.08) * mm});
            skLineSegment(sketch, "E330", {"start": v(158.47, -57.08) * mm, "end": v(155.21, -57.56) * mm});
            skLineSegment(sketch, "E331", {"start": v(155.21, -57.56) * mm, "end": v(155.7, -64.96) * mm});
            skLineSegment(sketch, "E332", {"start": v(0, 0) * mm, "end": v(866.03, -500) * mm, "construction": true});
            skLineSegment(sketch, "E333", {"start": v(0, 0) * mm, "end": v(0, 1000) * mm, "construction": true});
            skLineSegment(sketch, "E334", {"start": v(0, 0) * mm, "end": v(-866.03, -500) * mm, "construction": true});
            skLineSegment(sketch, "E335.1.0", {"start": v(-13.2, 174.33) * mm, "end": v(-12.3, 171.17) * mm});
            skLineSegment(sketch, "E335.1.1", {"start": v(-14.78, 177.07) * mm, "end": v(-13.2, 174.33) * mm});
            skLineSegment(sketch, "E335.1.2", {"start": v(-23.87, 180.42) * mm, "end": v(-19.95, 182.04) * mm});
            skLineSegment(sketch, "E335.1.3", {"start": v(48.74, 113.55) * mm, "end": v(53.7, 108.38) * mm});
            skLineSegment(sketch, "E335.1.4", {"start": v(34.87, 156.09) * mm, "end": v(38.98, 149.92) * mm});
            skLineSegment(sketch, "E335.1.5", {"start": v(-48.74, 143.12) * mm, "end": v(-53.7, 148.29) * mm});
            skLineSegment(sketch, "E335.1.6", {"start": v(53.7, 108.38) * mm, "end": v(52.09, 104.47) * mm});
            skLineSegment(sketch, "E335.1.7", {"start": v(38.98, 149.92) * mm, "end": v(41.87, 151.52) * mm});
            skLineSegment(sketch, "E335.1.8", {"start": v(12.3, 85.5) * mm, "end": v(5.03, 84.06) * mm});
            skLineSegment(sketch, "E335.1.9", {"start": v(38.98, 106.74) * mm, "end": v(34.87, 100.58) * mm});
            skLineSegment(sketch, "E335.1.10", {"start": v(-27.75, 163.2) * mm, "end": v(-21.6, 167.32) * mm});
            skLineSegment(sketch, "E335.1.11", {"start": v(21.6, 89.35) * mm, "end": v(23.19, 86.47) * mm});
            skLineSegment(sketch, "E335.1.12", {"start": v(34.87, 100.58) * mm, "end": v(37.44, 98.53) * mm});
            skLineSegment(sketch, "E335.1.13", {"start": v(29.8, 165.78) * mm, "end": v(32.3, 167.7) * mm});
            skLineSegment(sketch, "E335.1.14", {"start": v(-42.83, 116.03) * mm, "end": v(-44.28, 123.3) * mm});
            skLineSegment(sketch, "E335.1.15", {"start": v(-21.6, 89.35) * mm, "end": v(-27.75, 93.47) * mm});
            skLineSegment(sketch, "E335.1.16", {"start": v(42.83, 116.03) * mm, "end": v(46, 115.13) * mm});
            skLineSegment(sketch, "E335.1.17", {"start": v(44.28, 133.36) * mm, "end": v(47.55, 133.73) * mm});
            skLineSegment(sketch, "E335.1.18", {"start": v(47.55, 133.73) * mm, "end": v(50.68, 133.33) * mm});
            skLineSegment(sketch, "E335.1.19", {"start": v(-42.83, 140.63) * mm, "end": v(-46, 141.54) * mm});
            skLineSegment(sketch, "E335.1.20", {"start": v(-38.99, 86.35) * mm, "end": v(-41.98, 89.35) * mm});
            skLineSegment(sketch, "E335.1.21", {"start": v(-19.95, 182.04) * mm, "end": v(-14.78, 177.07) * mm});
            skLineSegment(sketch, "E335.1.22", {"start": v(12.3, 171.17) * mm, "end": v(13.2, 174.33) * mm});
            skLineSegment(sketch, "E335.1.23", {"start": v(5.03, 84.06) * mm, "end": v(5.4, 80.78) * mm});
            skLineSegment(sketch, "E335.1.24", {"start": v(-12.3, 171.17) * mm, "end": v(-5.03, 172.61) * mm});
            skLineSegment(sketch, "E335.1.25", {"start": v(39.37, 96.02) * mm, "end": v(41.98, 89.35) * mm});
            skLineSegment(sketch, "E335.1.26", {"start": v(-57.26, 130.45) * mm, "end": v(-50.68, 133.33) * mm});
            skLineSegment(sketch, "E335.1.27", {"start": v(52.09, 152.2) * mm, "end": v(53.7, 148.29) * mm});
            skLineSegment(sketch, "E335.1.28", {"start": v(-52.09, 152.2) * mm, "end": v(-44.92, 152.34) * mm});
            skLineSegment(sketch, "E335.1.29", {"start": v(41.98, 167.32) * mm, "end": v(39.37, 160.64) * mm});
            skLineSegment(sketch, "E335.1.30", {"start": v(57.26, 126.22) * mm, "end": v(50.68, 123.34) * mm});
            skLineSegment(sketch, "E335.1.31", {"start": v(53.7, 148.29) * mm, "end": v(48.74, 143.12) * mm});
            skLineSegment(sketch, "E335.1.32", {"start": v(-5, 179.02) * mm, "end": v(-2.12, 185.6) * mm});
            skLineSegment(sketch, "E335.1.33", {"start": v(52.09, 104.47) * mm, "end": v(44.92, 104.33) * mm});
            skLineSegment(sketch, "E335.1.34", {"start": v(57.26, 130.45) * mm, "end": v(57.26, 126.22) * mm});
            skLineSegment(sketch, "E335.1.35", {"start": v(-2.12, 185.6) * mm, "end": v(2.12, 185.6) * mm});
            skLineSegment(sketch, "E335.1.36", {"start": v(23.19, 86.47) * mm, "end": v(24, 83.42) * mm});
            skLineSegment(sketch, "E335.1.37", {"start": v(-21.6, 167.32) * mm, "end": v(-23.19, 170.2) * mm});
            skLineSegment(sketch, "E335.1.38", {"start": v(-24, 173.25) * mm, "end": v(-23.87, 180.42) * mm});
            skLineSegment(sketch, "E335.1.39", {"start": v(38.99, 170.32) * mm, "end": v(41.98, 167.32) * mm});
            skLineSegment(sketch, "E335.1.40", {"start": v(14.78, 177.07) * mm, "end": v(19.95, 182.04) * mm});
            skLineSegment(sketch, "E335.1.41", {"start": v(-53.7, 108.38) * mm, "end": v(-48.74, 113.55) * mm});
            skLineSegment(sketch, "E335.1.42", {"start": v(23.87, 180.42) * mm, "end": v(24, 173.25) * mm});
            skLineSegment(sketch, "E335.1.43", {"start": v(13.2, 174.33) * mm, "end": v(14.78, 177.07) * mm});
            skLineSegment(sketch, "E335.1.44", {"start": v(-53.7, 148.29) * mm, "end": v(-52.09, 152.2) * mm});
            skLineSegment(sketch, "E335.1.45", {"start": v(23.87, 76.25) * mm, "end": v(19.95, 74.62) * mm});
            skLineSegment(sketch, "E335.1.46", {"start": v(19.95, 182.04) * mm, "end": v(23.87, 180.42) * mm});
            skLineSegment(sketch, "E335.1.47", {"start": v(-32.3, 88.96) * mm, "end": v(-38.99, 86.35) * mm});
            skLineSegment(sketch, "E335.1.48", {"start": v(-44.92, 104.33) * mm, "end": v(-52.09, 104.47) * mm});
            skLineSegment(sketch, "E335.1.49", {"start": v(-14.78, 79.6) * mm, "end": v(-19.95, 74.62) * mm});
            skLineSegment(sketch, "E335.1.50", {"start": v(-44.28, 133.36) * mm, "end": v(-42.83, 140.63) * mm});
            skLineSegment(sketch, "E335.1.51", {"start": v(24, 83.42) * mm, "end": v(23.87, 76.25) * mm});
            skLineSegment(sketch, "E335.1.52", {"start": v(-50.68, 123.34) * mm, "end": v(-57.26, 126.22) * mm});
            skLineSegment(sketch, "E335.1.53", {"start": v(-38.98, 149.92) * mm, "end": v(-34.87, 156.09) * mm});
            skLineSegment(sketch, "E335.1.54", {"start": v(-37.44, 158.14) * mm, "end": v(-39.37, 160.64) * mm});
            skLineSegment(sketch, "E335.1.55", {"start": v(41.87, 151.52) * mm, "end": v(44.92, 152.34) * mm});
            skLineSegment(sketch, "E335.1.56", {"start": v(-19.95, 74.62) * mm, "end": v(-23.87, 76.25) * mm});
            skLineSegment(sketch, "E335.1.57", {"start": v(-52.09, 104.47) * mm, "end": v(-53.7, 108.38) * mm});
            skLineSegment(sketch, "E335.1.58", {"start": v(-47.55, 122.93) * mm, "end": v(-50.68, 123.34) * mm});
            skLineSegment(sketch, "E335.1.59", {"start": v(-29.8, 90.9) * mm, "end": v(-32.3, 88.96) * mm});
            skLineSegment(sketch, "E335.1.60", {"start": v(2.12, 185.6) * mm, "end": v(5, 179.02) * mm});
            skLineSegment(sketch, "E335.1.61", {"start": v(-41.87, 105.15) * mm, "end": v(-44.92, 104.33) * mm});
            skLineSegment(sketch, "E335.1.62", {"start": v(46, 115.13) * mm, "end": v(48.74, 113.55) * mm});
            skLineSegment(sketch, "E335.1.63", {"start": v(-46, 141.54) * mm, "end": v(-48.74, 143.12) * mm});
            skLineSegment(sketch, "E335.1.64", {"start": v(41.98, 89.35) * mm, "end": v(38.99, 86.35) * mm});
            skLineSegment(sketch, "E335.1.65", {"start": v(44.92, 152.34) * mm, "end": v(52.09, 152.2) * mm});
            skLineSegment(sketch, "E335.1.66", {"start": v(37.44, 98.53) * mm, "end": v(39.37, 96.02) * mm});
            skLineSegment(sketch, "E335.1.67", {"start": v(50.68, 133.33) * mm, "end": v(57.26, 130.45) * mm});
            skLineSegment(sketch, "E335.1.68", {"start": v(32.3, 167.7) * mm, "end": v(38.99, 170.32) * mm});
            skLineSegment(sketch, "E335.1.69", {"start": v(-39.37, 160.64) * mm, "end": v(-41.98, 167.32) * mm});
            skLineSegment(sketch, "E335.1.70", {"start": v(38.99, 86.35) * mm, "end": v(32.3, 88.96) * mm});
            skLineSegment(sketch, "E335.1.71", {"start": v(-57.26, 126.22) * mm, "end": v(-57.26, 130.45) * mm});
            skLineSegment(sketch, "E335.1.72", {"start": v(-44.28, 123.3) * mm, "end": v(-47.55, 122.93) * mm});
            skLineSegment(sketch, "E335.1.73", {"start": v(-27.75, 93.47) * mm, "end": v(-29.8, 90.9) * mm});
            skLineSegment(sketch, "E335.1.74", {"start": v(27.75, 163.2) * mm, "end": v(29.8, 165.78) * mm});
            skLineSegment(sketch, "E335.1.75", {"start": v(-34.87, 156.09) * mm, "end": v(-37.44, 158.14) * mm});
            skLineSegment(sketch, "E335.1.76", {"start": v(-41.98, 167.32) * mm, "end": v(-38.99, 170.32) * mm});
            skLineSegment(sketch, "E335.1.77", {"start": v(-41.98, 89.35) * mm, "end": v(-39.37, 96.02) * mm});
            skLineSegment(sketch, "E335.1.78", {"start": v(-38.99, 170.32) * mm, "end": v(-32.3, 167.7) * mm});
            skLineSegment(sketch, "E335.1.79", {"start": v(19.95, 74.62) * mm, "end": v(14.78, 79.6) * mm});
            skLineSegment(sketch, "E335.1.80", {"start": v(5.03, 172.61) * mm, "end": v(12.3, 171.17) * mm});
            skLineSegment(sketch, "E335.1.81", {"start": v(-23.19, 170.2) * mm, "end": v(-24, 173.25) * mm});
            skLineSegment(sketch, "E335.1.82", {"start": v(-38.98, 106.74) * mm, "end": v(-41.87, 105.15) * mm});
            skLineSegment(sketch, "E335.1.83", {"start": v(-48.74, 113.55) * mm, "end": v(-46, 115.13) * mm});
            skLineSegment(sketch, "E335.1.84", {"start": v(50.68, 123.34) * mm, "end": v(47.55, 122.93) * mm});
            skLineSegment(sketch, "E335.1.85", {"start": v(-32.3, 167.7) * mm, "end": v(-29.8, 165.78) * mm});
            skLineSegment(sketch, "E335.1.86", {"start": v(-50.68, 133.33) * mm, "end": v(-47.55, 133.73) * mm});
            skLineSegment(sketch, "E335.1.87", {"start": v(48.74, 143.12) * mm, "end": v(46, 141.54) * mm});
            skLineSegment(sketch, "E335.1.88", {"start": v(47.55, 122.93) * mm, "end": v(44.28, 123.3) * mm});
            skLineSegment(sketch, "E335.1.89", {"start": v(-41.87, 151.52) * mm, "end": v(-38.98, 149.92) * mm});
            skLineSegment(sketch, "E335.1.90", {"start": v(42.83, 140.63) * mm, "end": v(44.28, 133.36) * mm});
            skLineSegment(sketch, "E335.1.91", {"start": v(44.28, 123.3) * mm, "end": v(42.83, 116.03) * mm});
            skLineSegment(sketch, "E335.1.92", {"start": v(27.75, 93.47) * mm, "end": v(21.6, 89.35) * mm});
            skLineSegment(sketch, "E335.1.93", {"start": v(21.6, 167.32) * mm, "end": v(27.75, 163.2) * mm});
            skLineSegment(sketch, "E335.1.94", {"start": v(29.8, 90.9) * mm, "end": v(27.75, 93.47) * mm});
            skLineSegment(sketch, "E335.1.95", {"start": v(-5.03, 172.61) * mm, "end": v(-5.4, 175.89) * mm});
            skLineSegment(sketch, "E335.1.96", {"start": v(-44.92, 152.34) * mm, "end": v(-41.87, 151.52) * mm});
            skLineSegment(sketch, "E335.1.97", {"start": v(-39.37, 96.02) * mm, "end": v(-37.44, 98.53) * mm});
            skLineSegment(sketch, "E335.1.98", {"start": v(23.19, 170.2) * mm, "end": v(21.6, 167.32) * mm});
            skLineSegment(sketch, "E335.1.99", {"start": v(39.37, 160.64) * mm, "end": v(37.44, 158.14) * mm});
            skLineSegment(sketch, "E335.1.100", {"start": v(-46, 115.13) * mm, "end": v(-42.83, 116.03) * mm});
            skLineSegment(sketch, "E335.1.101", {"start": v(-5.4, 175.89) * mm, "end": v(-5, 179.02) * mm});
            skLineSegment(sketch, "E335.1.102", {"start": v(46, 141.54) * mm, "end": v(42.83, 140.63) * mm});
            skLineSegment(sketch, "E335.1.103", {"start": v(24, 173.25) * mm, "end": v(23.19, 170.2) * mm});
            skLineSegment(sketch, "E335.1.104", {"start": v(37.44, 158.14) * mm, "end": v(34.87, 156.09) * mm});
            skLineSegment(sketch, "E335.1.105", {"start": v(5, 179.02) * mm, "end": v(5.4, 175.89) * mm});
            skLineSegment(sketch, "E335.1.106", {"start": v(-34.87, 100.58) * mm, "end": v(-38.98, 106.74) * mm});
            skLineSegment(sketch, "E335.1.107", {"start": v(5.4, 175.89) * mm, "end": v(5.03, 172.61) * mm});
            skLineSegment(sketch, "E335.1.108", {"start": v(32.3, 88.96) * mm, "end": v(29.8, 90.9) * mm});
            skLineSegment(sketch, "E335.1.109", {"start": v(-29.8, 165.78) * mm, "end": v(-27.75, 163.2) * mm});
            skLineSegment(sketch, "E335.1.110", {"start": v(44.92, 104.33) * mm, "end": v(41.87, 105.15) * mm});
            skLineSegment(sketch, "E335.1.111", {"start": v(-37.44, 98.53) * mm, "end": v(-34.87, 100.58) * mm});
            skLineSegment(sketch, "E335.1.112", {"start": v(-47.55, 133.73) * mm, "end": v(-44.28, 133.36) * mm});
            skLineSegment(sketch, "E335.1.113", {"start": v(41.87, 105.15) * mm, "end": v(38.98, 106.74) * mm});
            skLineSegment(sketch, "E335.1.114", {"start": v(-24, 83.42) * mm, "end": v(-23.19, 86.47) * mm});
            skLineSegment(sketch, "E335.1.115", {"start": v(-23.19, 86.47) * mm, "end": v(-21.6, 89.35) * mm});
            skLineSegment(sketch, "E335.1.116", {"start": v(-12.3, 85.5) * mm, "end": v(-13.2, 82.33) * mm});
            skLineSegment(sketch, "E335.1.117", {"start": v(-13.2, 82.33) * mm, "end": v(-14.78, 79.6) * mm});
            skLineSegment(sketch, "E335.1.118", {"start": v(5, 77.65) * mm, "end": v(2.12, 71.08) * mm});
            skLineSegment(sketch, "E335.1.119", {"start": v(-23.87, 76.25) * mm, "end": v(-24, 83.42) * mm});
            skLineSegment(sketch, "E335.1.120", {"start": v(2.12, 71.08) * mm, "end": v(-2.12, 71.08) * mm});
            skLineSegment(sketch, "E335.1.121", {"start": v(5.4, 80.78) * mm, "end": v(5, 77.65) * mm});
            skLineSegment(sketch, "E335.1.122", {"start": v(-2.12, 71.08) * mm, "end": v(-5, 77.65) * mm});
            skLineSegment(sketch, "E335.1.123", {"start": v(-5.03, 84.06) * mm, "end": v(-12.3, 85.5) * mm});
            skLineSegment(sketch, "E335.1.124", {"start": v(13.2, 82.33) * mm, "end": v(12.3, 85.5) * mm});
            skLineSegment(sketch, "E335.1.125", {"start": v(14.78, 79.6) * mm, "end": v(13.2, 82.33) * mm});
            skLineSegment(sketch, "E335.1.126", {"start": v(-5, 77.65) * mm, "end": v(-5.4, 80.78) * mm});
            skLineSegment(sketch, "E335.1.127", {"start": v(-5.4, 80.78) * mm, "end": v(-5.03, 84.06) * mm});
            skLineSegment(sketch, "E335.2.0", {"start": v(-144.37, -98.6) * mm, "end": v(-142.08, -96.23) * mm});
            skLineSegment(sketch, "E335.2.1", {"start": v(-145.96, -101.34) * mm, "end": v(-144.37, -98.6) * mm});
            skLineSegment(sketch, "E335.2.2", {"start": v(-144.32, -110.88) * mm, "end": v(-147.68, -108.3) * mm});
            skLineSegment(sketch, "E335.2.3", {"start": v(-122.7, -14.57) * mm, "end": v(-120.71, -7.68) * mm});
            skLineSegment(sketch, "E335.2.4", {"start": v(-152.6, -47.85) * mm, "end": v(-149.33, -41.2) * mm});
            skLineSegment(sketch, "E335.2.5", {"start": v(-99.58, -113.77) * mm, "end": v(-101.57, -120.66) * mm});
            skLineSegment(sketch, "E335.2.6", {"start": v(-120.71, -7.68) * mm, "end": v(-116.51, -7.12) * mm});
            skLineSegment(sketch, "E335.2.7", {"start": v(-149.33, -41.2) * mm, "end": v(-152.15, -39.5) * mm});
            skLineSegment(sketch, "E335.2.8", {"start": v(-80.2, -32.1) * mm, "end": v(-75.3, -37.67) * mm});
            skLineSegment(sketch, "E335.2.9", {"start": v(-111.93, -19.61) * mm, "end": v(-104.54, -20.1) * mm});
            skLineSegment(sketch, "E335.2.10", {"start": v(-127.46, -105.64) * mm, "end": v(-134.1, -102.36) * mm});
            skLineSegment(sketch, "E335.2.11", {"start": v(-88.17, -25.98) * mm, "end": v(-86.48, -23.15) * mm});
            skLineSegment(sketch, "E335.2.12", {"start": v(-104.54, -20.1) * mm, "end": v(-104.05, -16.84) * mm});
            skLineSegment(sketch, "E335.2.13", {"start": v(-158.47, -57.08) * mm, "end": v(-161.39, -55.87) * mm});
            skLineSegment(sketch, "E335.2.14", {"start": v(-79.07, -95.11) * mm, "end": v(-84.65, -100) * mm});
            skLineSegment(sketch, "E335.2.15", {"start": v(-66.58, -63.37) * mm, "end": v(-67.07, -70.77) * mm});
            skLineSegment(sketch, "E335.2.16", {"start": v(-121.9, -20.92) * mm, "end": v(-122.7, -17.73) * mm});
            skLineSegment(sketch, "E335.2.17", {"start": v(-137.63, -28.33) * mm, "end": v(-139.6, -25.69) * mm});
            skLineSegment(sketch, "E335.2.18", {"start": v(-139.6, -25.69) * mm, "end": v(-140.8, -22.77) * mm});
            skLineSegment(sketch, "E335.2.19", {"start": v(-100.38, -107.41) * mm, "end": v(-99.58, -110.6) * mm});
            skLineSegment(sketch, "E335.2.20", {"start": v(-55.29, -76.94) * mm, "end": v(-56.38, -81.03) * mm});
            skLineSegment(sketch, "E335.2.21", {"start": v(-147.68, -108.3) * mm, "end": v(-145.96, -101.34) * mm});
            skLineSegment(sketch, "E335.2.22", {"start": v(-154.38, -74.93) * mm, "end": v(-157.58, -75.73) * mm});
            skLineSegment(sketch, "E335.2.23", {"start": v(-75.3, -37.67) * mm, "end": v(-72.66, -35.71) * mm});
            skLineSegment(sketch, "E335.2.24", {"start": v(-142.08, -96.23) * mm, "end": v(-146.97, -90.66) * mm});
            skLineSegment(sketch, "E335.2.25", {"start": v(-102.84, -13.92) * mm, "end": v(-98.37, -8.31) * mm});
            skLineSegment(sketch, "E335.2.26", {"start": v(-84.35, -114.81) * mm, "end": v(-90.12, -110.56) * mm});
            skLineSegment(sketch, "E335.2.27", {"start": v(-157.85, -31) * mm, "end": v(-155.28, -27.63) * mm});
            skLineSegment(sketch, "E335.2.28", {"start": v(-105.77, -121.21) * mm, "end": v(-109.47, -115.07) * mm});
            skLineSegment(sketch, "E335.2.29", {"start": v(-165.9, -47.3) * mm, "end": v(-158.8, -46.23) * mm});
            skLineSegment(sketch, "E335.2.30", {"start": v(-137.93, -13.52) * mm, "end": v(-132.16, -17.78) * mm});
            skLineSegment(sketch, "E335.2.31", {"start": v(-155.28, -27.63) * mm, "end": v(-148.31, -29.35) * mm});
            skLineSegment(sketch, "E335.2.32", {"start": v(-152.54, -93.83) * mm, "end": v(-159.67, -94.63) * mm});
            skLineSegment(sketch, "E335.2.33", {"start": v(-116.51, -7.12) * mm, "end": v(-112.8, -13.26) * mm});
            skLineSegment(sketch, "E335.2.34", {"start": v(-141.6, -15.64) * mm, "end": v(-137.93, -13.52) * mm});
            skLineSegment(sketch, "E335.2.35", {"start": v(-159.67, -94.63) * mm, "end": v(-161.79, -90.96) * mm});
            skLineSegment(sketch, "E335.2.36", {"start": v(-86.48, -23.15) * mm, "end": v(-84.25, -20.92) * mm});
            skLineSegment(sketch, "E335.2.37", {"start": v(-134.1, -102.36) * mm, "end": v(-135.8, -105.18) * mm});
            skLineSegment(sketch, "E335.2.38", {"start": v(-138.03, -107.42) * mm, "end": v(-144.32, -110.88) * mm});
            skLineSegment(sketch, "E335.2.39", {"start": v(-167, -51.4) * mm, "end": v(-165.9, -47.3) * mm});
            skLineSegment(sketch, "E335.2.40", {"start": v(-160.74, -75.73) * mm, "end": v(-167.63, -73.74) * mm});
            skLineSegment(sketch, "E335.2.41", {"start": v(-67, -100.7) * mm, "end": v(-73.97, -98.98) * mm});
            skLineSegment(sketch, "E335.2.42", {"start": v(-168.18, -69.54) * mm, "end": v(-162.04, -65.83) * mm});
            skLineSegment(sketch, "E335.2.43", {"start": v(-157.58, -75.73) * mm, "end": v(-160.74, -75.73) * mm});
            skLineSegment(sketch, "E335.2.44", {"start": v(-101.57, -120.66) * mm, "end": v(-105.77, -121.21) * mm});
            skLineSegment(sketch, "E335.2.45", {"start": v(-77.97, -17.45) * mm, "end": v(-74.6, -20.03) * mm});
            skLineSegment(sketch, "E335.2.46", {"start": v(-167.63, -73.74) * mm, "end": v(-168.18, -69.54) * mm});
            skLineSegment(sketch, "E335.2.47", {"start": v(-60.9, -72.46) * mm, "end": v(-55.29, -76.94) * mm});
            skLineSegment(sketch, "E335.2.48", {"start": v(-67.9, -91.06) * mm, "end": v(-64.43, -97.34) * mm});
            skLineSegment(sketch, "E335.2.49", {"start": v(-61.54, -52.6) * mm, "end": v(-54.65, -54.6) * mm});
            skLineSegment(sketch, "E335.2.50", {"start": v(-93.36, -105.03) * mm, "end": v(-100.38, -107.41) * mm});
            skLineSegment(sketch, "E335.2.51", {"start": v(-84.25, -20.92) * mm, "end": v(-77.97, -17.45) * mm});
            skLineSegment(sketch, "E335.2.52", {"start": v(-81.48, -105.56) * mm, "end": v(-80.68, -112.7) * mm});
            skLineSegment(sketch, "E335.2.53", {"start": v(-110.35, -108.72) * mm, "end": v(-117.74, -108.24) * mm});
            skLineSegment(sketch, "E335.2.54", {"start": v(-118.23, -111.5) * mm, "end": v(-119.44, -114.42) * mm});
            skLineSegment(sketch, "E335.2.55", {"start": v(-152.15, -39.5) * mm, "end": v(-154.39, -37.27) * mm});
            skLineSegment(sketch, "E335.2.56", {"start": v(-54.65, -54.6) * mm, "end": v(-54.1, -58.8) * mm});
            skLineSegment(sketch, "E335.2.57", {"start": v(-64.43, -97.34) * mm, "end": v(-67, -100.7) * mm});
            skLineSegment(sketch, "E335.2.58", {"start": v(-82.69, -102.65) * mm, "end": v(-81.48, -105.56) * mm});
            skLineSegment(sketch, "E335.2.59", {"start": v(-63.81, -71.26) * mm, "end": v(-60.9, -72.46) * mm});
            skLineSegment(sketch, "E335.2.60", {"start": v(-161.79, -90.96) * mm, "end": v(-157.53, -85.19) * mm});
            skLineSegment(sketch, "E335.2.61", {"start": v(-70.13, -88.83) * mm, "end": v(-67.9, -91.06) * mm});
            skLineSegment(sketch, "E335.2.62", {"start": v(-122.7, -17.73) * mm, "end": v(-122.7, -14.57) * mm});
            skLineSegment(sketch, "E335.2.63", {"start": v(-99.58, -110.6) * mm, "end": v(-99.58, -113.77) * mm});
            skLineSegment(sketch, "E335.2.64", {"start": v(-98.37, -8.31) * mm, "end": v(-94.27, -9.4) * mm});
            skLineSegment(sketch, "E335.2.65", {"start": v(-154.39, -37.27) * mm, "end": v(-157.85, -31) * mm});
            skLineSegment(sketch, "E335.2.66", {"start": v(-104.05, -16.84) * mm, "end": v(-102.84, -13.92) * mm});
            skLineSegment(sketch, "E335.2.67", {"start": v(-140.8, -22.77) * mm, "end": v(-141.6, -15.64) * mm});
            skLineSegment(sketch, "E335.2.68", {"start": v(-161.39, -55.87) * mm, "end": v(-167, -51.4) * mm});
            skLineSegment(sketch, "E335.2.69", {"start": v(-119.44, -114.42) * mm, "end": v(-123.91, -120.02) * mm});
            skLineSegment(sketch, "E335.2.70", {"start": v(-94.27, -9.4) * mm, "end": v(-93.2, -16.5) * mm});
            skLineSegment(sketch, "E335.2.71", {"start": v(-80.68, -112.7) * mm, "end": v(-84.35, -114.81) * mm});
            skLineSegment(sketch, "E335.2.72", {"start": v(-84.65, -100) * mm, "end": v(-82.69, -102.65) * mm});
            skLineSegment(sketch, "E335.2.73", {"start": v(-67.07, -70.77) * mm, "end": v(-63.81, -71.26) * mm});
            skLineSegment(sketch, "E335.2.74", {"start": v(-155.21, -57.56) * mm, "end": v(-158.47, -57.08) * mm});
            skLineSegment(sketch, "E335.2.75", {"start": v(-117.74, -108.24) * mm, "end": v(-118.23, -111.5) * mm});
            skLineSegment(sketch, "E335.2.76", {"start": v(-123.91, -120.02) * mm, "end": v(-128, -118.92) * mm});
            skLineSegment(sketch, "E335.2.77", {"start": v(-56.38, -81.03) * mm, "end": v(-63.48, -82.1) * mm});
            skLineSegment(sketch, "E335.2.78", {"start": v(-128, -118.92) * mm, "end": v(-129.08, -111.83) * mm});
            skLineSegment(sketch, "E335.2.79", {"start": v(-74.6, -20.03) * mm, "end": v(-76.33, -27) * mm});
            skLineSegment(sketch, "E335.2.80", {"start": v(-152, -81.95) * mm, "end": v(-154.38, -74.93) * mm});
            skLineSegment(sketch, "E335.2.81", {"start": v(-135.8, -105.18) * mm, "end": v(-138.03, -107.42) * mm});
            skLineSegment(sketch, "E335.2.82", {"start": v(-72.95, -87.13) * mm, "end": v(-70.13, -88.83) * mm});
            skLineSegment(sketch, "E335.2.83", {"start": v(-73.97, -98.98) * mm, "end": v(-76.7, -97.4) * mm});
            skLineSegment(sketch, "E335.2.84", {"start": v(-132.16, -17.78) * mm, "end": v(-130.24, -20.29) * mm});
            skLineSegment(sketch, "E335.2.85", {"start": v(-129.08, -111.83) * mm, "end": v(-128.66, -108.7) * mm});
            skLineSegment(sketch, "E335.2.86", {"start": v(-90.12, -110.56) * mm, "end": v(-92.04, -108.05) * mm});
            skLineSegment(sketch, "E335.2.87", {"start": v(-148.31, -29.35) * mm, "end": v(-145.58, -30.93) * mm});
            skLineSegment(sketch, "E335.2.88", {"start": v(-130.24, -20.29) * mm, "end": v(-128.92, -23.3) * mm});
            skLineSegment(sketch, "E335.2.89", {"start": v(-110.29, -112.02) * mm, "end": v(-110.35, -108.72) * mm});
            skLineSegment(sketch, "E335.2.90", {"start": v(-143.2, -33.22) * mm, "end": v(-137.63, -28.33) * mm});
            skLineSegment(sketch, "E335.2.91", {"start": v(-128.92, -23.3) * mm, "end": v(-121.9, -20.92) * mm});
            skLineSegment(sketch, "E335.2.92", {"start": v(-94.82, -22.7) * mm, "end": v(-88.17, -25.98) * mm});
            skLineSegment(sketch, "E335.2.93", {"start": v(-155.7, -64.96) * mm, "end": v(-155.21, -57.56) * mm});
            skLineSegment(sketch, "E335.2.94", {"start": v(-93.62, -19.63) * mm, "end": v(-94.82, -22.7) * mm});
            skLineSegment(sketch, "E335.2.95", {"start": v(-146.97, -90.66) * mm, "end": v(-149.62, -92.62) * mm});
            skLineSegment(sketch, "E335.2.96", {"start": v(-109.47, -115.07) * mm, "end": v(-110.29, -112.02) * mm});
            skLineSegment(sketch, "E335.2.97", {"start": v(-63.48, -82.1) * mm, "end": v(-66.6, -81.7) * mm});
            skLineSegment(sketch, "E335.2.98", {"start": v(-159, -65.02) * mm, "end": v(-155.7, -64.96) * mm});
            skLineSegment(sketch, "E335.2.99", {"start": v(-158.8, -46.23) * mm, "end": v(-155.67, -46.64) * mm});
            skLineSegment(sketch, "E335.2.100", {"start": v(-76.7, -97.4) * mm, "end": v(-79.07, -95.11) * mm});
            skLineSegment(sketch, "E335.2.101", {"start": v(-149.62, -92.62) * mm, "end": v(-152.54, -93.83) * mm});
            skLineSegment(sketch, "E335.2.102", {"start": v(-145.58, -30.93) * mm, "end": v(-143.2, -33.22) * mm});
            skLineSegment(sketch, "E335.2.103", {"start": v(-162.04, -65.83) * mm, "end": v(-159, -65.02) * mm});
            skLineSegment(sketch, "E335.2.104", {"start": v(-155.67, -46.64) * mm, "end": v(-152.6, -47.85) * mm});
            skLineSegment(sketch, "E335.2.105", {"start": v(-157.53, -85.19) * mm, "end": v(-155.02, -83.27) * mm});
            skLineSegment(sketch, "E335.2.106", {"start": v(-69.67, -80.48) * mm, "end": v(-72.95, -87.13) * mm});
            skLineSegment(sketch, "E335.2.107", {"start": v(-155.02, -83.27) * mm, "end": v(-152, -81.95) * mm});
            skLineSegment(sketch, "E335.2.108", {"start": v(-93.2, -16.5) * mm, "end": v(-93.62, -19.63) * mm});
            skLineSegment(sketch, "E335.2.109", {"start": v(-128.66, -108.7) * mm, "end": v(-127.46, -105.64) * mm});
            skLineSegment(sketch, "E335.2.110", {"start": v(-112.8, -13.26) * mm, "end": v(-112, -16.32) * mm});
            skLineSegment(sketch, "E335.2.111", {"start": v(-66.6, -81.7) * mm, "end": v(-69.67, -80.48) * mm});
            skLineSegment(sketch, "E335.2.112", {"start": v(-92.04, -108.05) * mm, "end": v(-93.36, -105.03) * mm});
            skLineSegment(sketch, "E335.2.113", {"start": v(-112, -16.32) * mm, "end": v(-111.93, -19.61) * mm});
            skLineSegment(sketch, "E335.2.114", {"start": v(-60.24, -62.5) * mm, "end": v(-63.29, -63.31) * mm});
            skLineSegment(sketch, "E335.2.115", {"start": v(-63.29, -63.31) * mm, "end": v(-66.58, -63.37) * mm});
            skLineSegment(sketch, "E335.2.116", {"start": v(-67.9, -53.4) * mm, "end": v(-64.7, -52.6) * mm});
            skLineSegment(sketch, "E335.2.117", {"start": v(-64.7, -52.6) * mm, "end": v(-61.54, -52.6) * mm});
            skLineSegment(sketch, "E335.2.118", {"start": v(-69.74, -34.5) * mm, "end": v(-62.61, -33.7) * mm});
            skLineSegment(sketch, "E335.2.119", {"start": v(-54.1, -58.8) * mm, "end": v(-60.24, -62.5) * mm});
            skLineSegment(sketch, "E335.2.120", {"start": v(-62.61, -33.7) * mm, "end": v(-60.5, -37.37) * mm});
            skLineSegment(sketch, "E335.2.121", {"start": v(-72.66, -35.71) * mm, "end": v(-69.74, -34.5) * mm});
            skLineSegment(sketch, "E335.2.122", {"start": v(-60.5, -37.37) * mm, "end": v(-64.75, -43.15) * mm});
            skLineSegment(sketch, "E335.2.123", {"start": v(-70.28, -46.38) * mm, "end": v(-67.9, -53.4) * mm});
            skLineSegment(sketch, "E335.2.124", {"start": v(-77.9, -29.73) * mm, "end": v(-80.2, -32.1) * mm});
            skLineSegment(sketch, "E335.2.125", {"start": v(-76.33, -27) * mm, "end": v(-77.9, -29.73) * mm});
            skLineSegment(sketch, "E335.2.126", {"start": v(-64.75, -43.15) * mm, "end": v(-67.26, -45.07) * mm});
            skLineSegment(sketch, "E335.2.127", {"start": v(-67.26, -45.07) * mm, "end": v(-70.28, -46.38) * mm});
            skPoint(sketch, "E335.center", {"position": v(0, 0) * mm});
            skCircle(sketch, "E336", {"center": v(-111.14, -64.17) * mm, "radius": 12.5 * mm});
            skCircle(sketch, "E337", {"center": v(111.14, -64.17) * mm, "radius": 12.5 * mm});
            skCircle(sketch, "E338", {"center": v(0, 128.33) * mm, "radius": 12.5 * mm});
            skLineSegment(sketch, "E339", {"start": v(-111.14, -64.17) * mm, "end": v(0, 0) * mm});
            skLineSegment(sketch, "E340", {"start": v(0, 128.33) * mm, "end": v(0, 0) * mm});
            skLineSegment(sketch, "E341", {"start": v(0, 0) * mm, "end": v(111.14, -64.17) * mm});
            skSolve(sketch);
        }
        {
            var Q0;
            Q0=qCreatedBy(makeId("Top.planeOp"),FACE);
            var sketch = newSketch(context, id + "F3", { "sketchPlane" : qUnion([Q0])});
            skLineSegment(sketch, "E342", {"start": v(0, 0) * mm, "end": v(866.03, -500) * mm, "construction": true});
            skLineSegment(sketch, "E343", {"start": v(0, 0) * mm, "end": v(0, 1000) * mm, "construction": true});
            skLineSegment(sketch, "E344", {"start": v(0, 0) * mm, "end": v(-866.03, -500) * mm, "construction": true});
            skLineSegment(sketch, "E345", {"start": v(339.85, -138.22) * mm, "end": v(340.08, -138.22) * mm});
            skLineSegment(sketch, "E346", {"start": v(340.08, -138.22) * mm, "end": v(346.25, -139.55) * mm});
            skLineSegment(sketch, "E347", {"start": v(346.25, -139.55) * mm, "end": v(352.62, -142.4) * mm});
            skLineSegment(sketch, "E348", {"start": v(352.62, -142.4) * mm, "end": v(352.46, -147.13) * mm});
            skLineSegment(sketch, "E349", {"start": v(352.46, -147.13) * mm, "end": v(345.91, -149.54) * mm});
            skLineSegment(sketch, "E350", {"start": v(345.91, -149.54) * mm, "end": v(339.66, -150.45) * mm});
            skLineSegment(sketch, "E351", {"start": v(339.66, -150.45) * mm, "end": v(339.44, -150.43) * mm});
            skLineSegment(sketch, "E352", {"start": v(339.44, -150.43) * mm, "end": v(338.58, -156.9) * mm});
            skLineSegment(sketch, "E353", {"start": v(338.58, -156.9) * mm, "end": v(338.8, -156.94) * mm});
            skLineSegment(sketch, "E354", {"start": v(338.8, -156.94) * mm, "end": v(344.6, -159.45) * mm});
            skLineSegment(sketch, "E355", {"start": v(344.6, -159.45) * mm, "end": v(350.29, -163.49) * mm});
            skLineSegment(sketch, "E356", {"start": v(350.29, -163.49) * mm, "end": v(349.21, -168.1) * mm});
            skLineSegment(sketch, "E357", {"start": v(349.21, -168.1) * mm, "end": v(342.32, -169.18) * mm});
            skLineSegment(sketch, "E358", {"start": v(342.32, -169.18) * mm, "end": v(336, -168.85) * mm});
            skLineSegment(sketch, "E359", {"start": v(336, -168.85) * mm, "end": v(335.8, -168.8) * mm});
            skLineSegment(sketch, "E360", {"start": v(335.8, -168.8) * mm, "end": v(333.7, -174.97) * mm});
            skLineSegment(sketch, "E361", {"start": v(333.7, -174.97) * mm, "end": v(333.9, -175.05) * mm});
            skLineSegment(sketch, "E362", {"start": v(333.9, -175.05) * mm, "end": v(339.1, -178.64) * mm});
            skLineSegment(sketch, "E363", {"start": v(339.1, -178.64) * mm, "end": v(343.89, -183.71) * mm});
            skLineSegment(sketch, "E364", {"start": v(343.89, -183.71) * mm, "end": v(341.93, -188.02) * mm});
            skLineSegment(sketch, "E365", {"start": v(341.93, -188.02) * mm, "end": v(334.96, -187.74) * mm});
            skLineSegment(sketch, "E366", {"start": v(334.96, -187.74) * mm, "end": v(328.83, -186.2) * mm});
            skLineSegment(sketch, "E367", {"start": v(328.83, -186.2) * mm, "end": v(328.64, -186.09) * mm});
            skLineSegment(sketch, "E368", {"start": v(328.64, -186.09) * mm, "end": v(325.37, -191.74) * mm});
            skLineSegment(sketch, "E369", {"start": v(325.37, -191.74) * mm, "end": v(325.56, -191.86) * mm});
            skLineSegment(sketch, "E370", {"start": v(325.56, -191.86) * mm, "end": v(329.95, -196.4) * mm});
            skLineSegment(sketch, "E371", {"start": v(329.95, -196.4) * mm, "end": v(333.66, -202.3) * mm});
            skLineSegment(sketch, "E372", {"start": v(333.66, -202.3) * mm, "end": v(330.9, -206.14) * mm});
            skLineSegment(sketch, "E373", {"start": v(330.9, -206.14) * mm, "end": v(324.12, -204.51) * mm});
            skLineSegment(sketch, "E374", {"start": v(324.12, -204.51) * mm, "end": v(318.42, -201.8) * mm});
            skLineSegment(sketch, "E375", {"start": v(318.42, -201.8) * mm, "end": v(318.24, -201.66) * mm});
            skLineSegment(sketch, "E376", {"start": v(318.24, -201.66) * mm, "end": v(313.93, -206.56) * mm});
            skLineSegment(sketch, "E377", {"start": v(313.93, -206.56) * mm, "end": v(314.1, -206.71) * mm});
            skLineSegment(sketch, "E378", {"start": v(314.1, -206.71) * mm, "end": v(317.52, -212.02) * mm});
            skLineSegment(sketch, "E379", {"start": v(317.52, -212.02) * mm, "end": v(320.01, -218.54) * mm});
            skLineSegment(sketch, "E380", {"start": v(320.01, -218.54) * mm, "end": v(316.56, -221.77) * mm});
            skLineSegment(sketch, "E381", {"start": v(316.56, -221.77) * mm, "end": v(310.22, -218.85) * mm});
            skLineSegment(sketch, "E382", {"start": v(310.22, -218.85) * mm, "end": v(305.15, -215.07) * mm});
            skLineSegment(sketch, "E383", {"start": v(305.15, -215.07) * mm, "end": v(305.01, -214.9) * mm});
            skLineSegment(sketch, "E384", {"start": v(305.01, -214.9) * mm, "end": v(299.83, -218.87) * mm});
            skLineSegment(sketch, "E385", {"start": v(299.83, -218.87) * mm, "end": v(299.96, -219.05) * mm});
            skLineSegment(sketch, "E386", {"start": v(299.96, -219.05) * mm, "end": v(302.28, -224.92) * mm});
            skLineSegment(sketch, "E387", {"start": v(302.28, -224.92) * mm, "end": v(303.45, -231.8) * mm});
            skLineSegment(sketch, "E388", {"start": v(303.45, -231.8) * mm, "end": v(299.43, -234.3) * mm});
            skLineSegment(sketch, "E389", {"start": v(299.43, -234.3) * mm, "end": v(293.79, -230.2) * mm});
            skLineSegment(sketch, "E390", {"start": v(293.79, -230.2) * mm, "end": v(289.56, -225.5) * mm});
            skLineSegment(sketch, "E391", {"start": v(289.56, -225.5) * mm, "end": v(289.45, -225.3) * mm});
            skLineSegment(sketch, "E392", {"start": v(289.45, -225.3) * mm, "end": v(283.6, -228.19) * mm});
            skLineSegment(sketch, "E393", {"start": v(283.6, -228.19) * mm, "end": v(283.69, -228.39) * mm});
            skLineSegment(sketch, "E394", {"start": v(283.69, -228.39) * mm, "end": v(284.82, -234.6) * mm});
            skLineSegment(sketch, "E395", {"start": v(284.82, -234.6) * mm, "end": v(284.62, -241.58) * mm});
            skLineSegment(sketch, "E396", {"start": v(284.62, -241.58) * mm, "end": v(280.2, -243.24) * mm});
            skLineSegment(sketch, "E397", {"start": v(280.2, -243.24) * mm, "end": v(275.46, -238.12) * mm});
            skLineSegment(sketch, "E398", {"start": v(275.46, -238.12) * mm, "end": v(272.22, -232.69) * mm});
            skLineSegment(sketch, "E399", {"start": v(272.22, -232.69) * mm, "end": v(272.16, -232.48) * mm});
            skLineSegment(sketch, "E400", {"start": v(272.16, -232.48) * mm, "end": v(265.85, -234.16) * mm});
            skLineSegment(sketch, "E401", {"start": v(265.85, -234.16) * mm, "end": v(265.9, -234.38) * mm});
            skLineSegment(sketch, "E402", {"start": v(265.9, -234.38) * mm, "end": v(265.8, -240.7) * mm});
            skLineSegment(sketch, "E403", {"start": v(265.8, -240.7) * mm, "end": v(264.25, -247.5) * mm});
            skLineSegment(sketch, "E404", {"start": v(264.25, -247.5) * mm, "end": v(259.58, -248.26) * mm});
            skLineSegment(sketch, "E405", {"start": v(259.58, -248.26) * mm, "end": v(255.94, -242.31) * mm});
            skLineSegment(sketch, "E406", {"start": v(255.94, -242.31) * mm, "end": v(253.82, -236.36) * mm});
            skLineSegment(sketch, "E407", {"start": v(253.82, -236.36) * mm, "end": v(253.8, -236.14) * mm});
            skLineSegment(sketch, "E408", {"start": v(253.8, -236.14) * mm, "end": v(247.29, -236.56) * mm});
            skLineSegment(sketch, "E409", {"start": v(247.29, -236.56) * mm, "end": v(247.3, -236.78) * mm});
            skLineSegment(sketch, "E410", {"start": v(247.3, -236.78) * mm, "end": v(245.96, -242.95) * mm});
            skLineSegment(sketch, "E411", {"start": v(245.96, -242.95) * mm, "end": v(243.11, -249.32) * mm});
            skLineSegment(sketch, "E412", {"start": v(243.11, -249.32) * mm, "end": v(238.38, -249.16) * mm});
            skLineSegment(sketch, "E413", {"start": v(238.38, -249.16) * mm, "end": v(235.97, -242.62) * mm});
            skLineSegment(sketch, "E414", {"start": v(235.97, -242.62) * mm, "end": v(235.06, -236.37) * mm});
            skLineSegment(sketch, "E415", {"start": v(235.06, -236.37) * mm, "end": v(235.08, -236.14) * mm});
            skLineSegment(sketch, "E416", {"start": v(235.08, -236.14) * mm, "end": v(228.6, -235.28) * mm});
            skLineSegment(sketch, "E417", {"start": v(228.6, -235.28) * mm, "end": v(228.57, -235.5) * mm});
            skLineSegment(sketch, "E418", {"start": v(228.57, -235.5) * mm, "end": v(226.06, -241.3) * mm});
            skLineSegment(sketch, "E419", {"start": v(226.06, -241.3) * mm, "end": v(222.02, -247) * mm});
            skLineSegment(sketch, "E420", {"start": v(222.02, -247) * mm, "end": v(217.42, -245.91) * mm});
            skLineSegment(sketch, "E421", {"start": v(217.42, -245.91) * mm, "end": v(216.33, -239.02) * mm});
            skLineSegment(sketch, "E422", {"start": v(216.33, -239.02) * mm, "end": v(216.65, -232.71) * mm});
            skLineSegment(sketch, "E423", {"start": v(216.65, -232.71) * mm, "end": v(216.72, -232.5) * mm});
            skLineSegment(sketch, "E424", {"start": v(216.72, -232.5) * mm, "end": v(210.54, -230.4) * mm});
            skLineSegment(sketch, "E425", {"start": v(210.54, -230.4) * mm, "end": v(210.46, -230.6) * mm});
            skLineSegment(sketch, "E426", {"start": v(210.46, -230.6) * mm, "end": v(206.87, -235.8) * mm});
            skLineSegment(sketch, "E427", {"start": v(206.87, -235.8) * mm, "end": v(201.8, -240.6) * mm});
            skLineSegment(sketch, "E428", {"start": v(201.8, -240.6) * mm, "end": v(197.5, -238.64) * mm});
            skLineSegment(sketch, "E429", {"start": v(197.5, -238.64) * mm, "end": v(197.77, -231.66) * mm});
            skLineSegment(sketch, "E430", {"start": v(197.77, -231.66) * mm, "end": v(199.32, -225.54) * mm});
            skLineSegment(sketch, "E431", {"start": v(199.32, -225.54) * mm, "end": v(199.42, -225.34) * mm});
            skLineSegment(sketch, "E432", {"start": v(199.42, -225.34) * mm, "end": v(193.77, -222.07) * mm});
            skLineSegment(sketch, "E433", {"start": v(193.77, -222.07) * mm, "end": v(193.65, -222.26) * mm});
            skLineSegment(sketch, "E434", {"start": v(193.65, -222.26) * mm, "end": v(189.12, -226.65) * mm});
            skLineSegment(sketch, "E435", {"start": v(189.12, -226.65) * mm, "end": v(183.2, -230.37) * mm});
            skLineSegment(sketch, "E436", {"start": v(183.2, -230.37) * mm, "end": v(179.36, -227.6) * mm});
            skLineSegment(sketch, "E437", {"start": v(179.36, -227.6) * mm, "end": v(181, -220.82) * mm});
            skLineSegment(sketch, "E438", {"start": v(181, -220.82) * mm, "end": v(183.71, -215.12) * mm});
            skLineSegment(sketch, "E439", {"start": v(183.71, -215.12) * mm, "end": v(183.85, -214.95) * mm});
            skLineSegment(sketch, "E440", {"start": v(183.85, -214.95) * mm, "end": v(178.95, -210.64) * mm});
            skLineSegment(sketch, "E441", {"start": v(178.95, -210.64) * mm, "end": v(178.8, -210.8) * mm});
            skLineSegment(sketch, "E442", {"start": v(178.8, -210.8) * mm, "end": v(173.49, -214.22) * mm});
            skLineSegment(sketch, "E443", {"start": v(173.49, -214.22) * mm, "end": v(166.97, -216.71) * mm});
            skLineSegment(sketch, "E444", {"start": v(166.97, -216.71) * mm, "end": v(163.74, -213.26) * mm});
            skLineSegment(sketch, "E445", {"start": v(163.74, -213.26) * mm, "end": v(166.66, -206.92) * mm});
            skLineSegment(sketch, "E446", {"start": v(166.66, -206.92) * mm, "end": v(170.44, -201.86) * mm});
            skLineSegment(sketch, "E447", {"start": v(170.44, -201.86) * mm, "end": v(170.6, -201.72) * mm});
            skLineSegment(sketch, "E448", {"start": v(170.6, -201.72) * mm, "end": v(166.64, -196.53) * mm});
            skLineSegment(sketch, "E449", {"start": v(166.64, -196.53) * mm, "end": v(166.46, -196.66) * mm});
            skLineSegment(sketch, "E450", {"start": v(166.46, -196.66) * mm, "end": v(160.59, -198.98) * mm});
            skLineSegment(sketch, "E451", {"start": v(160.59, -198.98) * mm, "end": v(153.7, -200.15) * mm});
            skLineSegment(sketch, "E452", {"start": v(153.7, -200.15) * mm, "end": v(151.21, -196.14) * mm});
            skLineSegment(sketch, "E453", {"start": v(151.21, -196.14) * mm, "end": v(155.32, -190.5) * mm});
            skLineSegment(sketch, "E454", {"start": v(155.32, -190.5) * mm, "end": v(160, -186.26) * mm});
            skLineSegment(sketch, "E455", {"start": v(160, -186.26) * mm, "end": v(160.2, -186.15) * mm});
            skLineSegment(sketch, "E456", {"start": v(160.2, -186.15) * mm, "end": v(157.32, -180.3) * mm});
            skLineSegment(sketch, "E457", {"start": v(157.32, -180.3) * mm, "end": v(157.12, -180.39) * mm});
            skLineSegment(sketch, "E458", {"start": v(157.12, -180.39) * mm, "end": v(150.9, -181.52) * mm});
            skLineSegment(sketch, "E459", {"start": v(150.9, -181.52) * mm, "end": v(143.93, -181.33) * mm});
            skLineSegment(sketch, "E460", {"start": v(143.93, -181.33) * mm, "end": v(142.27, -176.9) * mm});
            skLineSegment(sketch, "E461", {"start": v(142.27, -176.9) * mm, "end": v(147.4, -172.16) * mm});
            skLineSegment(sketch, "E462", {"start": v(147.4, -172.16) * mm, "end": v(152.82, -168.93) * mm});
            skLineSegment(sketch, "E463", {"start": v(152.82, -168.93) * mm, "end": v(153.03, -168.86) * mm});
            skLineSegment(sketch, "E464", {"start": v(153.03, -168.86) * mm, "end": v(151.35, -162.56) * mm});
            skLineSegment(sketch, "E465", {"start": v(151.35, -162.56) * mm, "end": v(151.13, -162.6) * mm});
            skLineSegment(sketch, "E466", {"start": v(151.13, -162.6) * mm, "end": v(144.82, -162.5) * mm});
            skLineSegment(sketch, "E467", {"start": v(144.82, -162.5) * mm, "end": v(138.01, -160.95) * mm});
            skLineSegment(sketch, "E468", {"start": v(138.01, -160.95) * mm, "end": v(137.25, -156.28) * mm});
            skLineSegment(sketch, "E469", {"start": v(137.25, -156.28) * mm, "end": v(143.2, -152.64) * mm});
            skLineSegment(sketch, "E470", {"start": v(143.2, -152.64) * mm, "end": v(149.15, -150.53) * mm});
            skLineSegment(sketch, "E471", {"start": v(149.15, -150.53) * mm, "end": v(149.37, -150.5) * mm});
            skLineSegment(sketch, "E472", {"start": v(149.37, -150.5) * mm, "end": v(148.95, -143.99) * mm});
            skLineSegment(sketch, "E473", {"start": v(148.95, -143.99) * mm, "end": v(148.73, -144) * mm});
            skLineSegment(sketch, "E474", {"start": v(148.73, -144) * mm, "end": v(142.56, -142.66) * mm});
            skLineSegment(sketch, "E475", {"start": v(142.56, -142.66) * mm, "end": v(136.19, -139.81) * mm});
            skLineSegment(sketch, "E476", {"start": v(136.19, -139.81) * mm, "end": v(136.35, -135.09) * mm});
            skLineSegment(sketch, "E477", {"start": v(136.35, -135.09) * mm, "end": v(142.9, -132.67) * mm});
            skLineSegment(sketch, "E478", {"start": v(142.9, -132.67) * mm, "end": v(149.14, -131.76) * mm});
            skLineSegment(sketch, "E479", {"start": v(149.14, -131.76) * mm, "end": v(149.37, -131.78) * mm});
            skLineSegment(sketch, "E480", {"start": v(149.37, -131.78) * mm, "end": v(150.22, -125.31) * mm});
            skLineSegment(sketch, "E481", {"start": v(150.22, -125.31) * mm, "end": v(150, -125.28) * mm});
            skLineSegment(sketch, "E482", {"start": v(150, -125.28) * mm, "end": v(144.2, -122.76) * mm});
            skLineSegment(sketch, "E483", {"start": v(144.2, -122.76) * mm, "end": v(138.52, -118.73) * mm});
            skLineSegment(sketch, "E484", {"start": v(138.52, -118.73) * mm, "end": v(139.6, -114.12) * mm});
            skLineSegment(sketch, "E485", {"start": v(139.6, -114.12) * mm, "end": v(146.49, -113.03) * mm});
            skLineSegment(sketch, "E486", {"start": v(146.49, -113.03) * mm, "end": v(152.8, -113.36) * mm});
            skLineSegment(sketch, "E487", {"start": v(152.8, -113.36) * mm, "end": v(153.01, -113.42) * mm});
            skLineSegment(sketch, "E488", {"start": v(153.01, -113.42) * mm, "end": v(155.12, -107.24) * mm});
            skLineSegment(sketch, "E489", {"start": v(155.12, -107.24) * mm, "end": v(154.9, -107.16) * mm});
            skLineSegment(sketch, "E490", {"start": v(154.9, -107.16) * mm, "end": v(149.71, -103.57) * mm});
            skLineSegment(sketch, "E491", {"start": v(149.71, -103.57) * mm, "end": v(144.92, -98.5) * mm});
            skLineSegment(sketch, "E492", {"start": v(144.92, -98.5) * mm, "end": v(146.87, -94.2) * mm});
            skLineSegment(sketch, "E493", {"start": v(146.87, -94.2) * mm, "end": v(153.85, -94.47) * mm});
            skLineSegment(sketch, "E494", {"start": v(153.85, -94.47) * mm, "end": v(159.97, -96.02) * mm});
            skLineSegment(sketch, "E495", {"start": v(159.97, -96.02) * mm, "end": v(160.17, -96.12) * mm});
            skLineSegment(sketch, "E496", {"start": v(160.17, -96.12) * mm, "end": v(163.44, -90.47) * mm});
            skLineSegment(sketch, "E497", {"start": v(163.44, -90.47) * mm, "end": v(163.25, -90.36) * mm});
            skLineSegment(sketch, "E498", {"start": v(163.25, -90.36) * mm, "end": v(158.85, -85.82) * mm});
            skLineSegment(sketch, "E499", {"start": v(158.85, -85.82) * mm, "end": v(155.14, -79.9) * mm});
            skLineSegment(sketch, "E500", {"start": v(155.14, -79.9) * mm, "end": v(157.9, -76.07) * mm});
            skLineSegment(sketch, "E501", {"start": v(157.9, -76.07) * mm, "end": v(164.69, -77.7) * mm});
            skLineSegment(sketch, "E502", {"start": v(164.69, -77.7) * mm, "end": v(170.39, -80.41) * mm});
            skLineSegment(sketch, "E503", {"start": v(170.39, -80.41) * mm, "end": v(170.56, -80.56) * mm});
            skLineSegment(sketch, "E504", {"start": v(170.56, -80.56) * mm, "end": v(174.87, -75.65) * mm});
            skLineSegment(sketch, "E505", {"start": v(174.87, -75.65) * mm, "end": v(174.7, -75.5) * mm});
            skLineSegment(sketch, "E506", {"start": v(174.7, -75.5) * mm, "end": v(171.28, -70.2) * mm});
            skLineSegment(sketch, "E507", {"start": v(171.28, -70.2) * mm, "end": v(168.8, -63.67) * mm});
            skLineSegment(sketch, "E508", {"start": v(168.8, -63.67) * mm, "end": v(172.25, -60.44) * mm});
            skLineSegment(sketch, "E509", {"start": v(172.25, -60.44) * mm, "end": v(178.59, -63.37) * mm});
            skLineSegment(sketch, "E510", {"start": v(178.59, -63.37) * mm, "end": v(183.65, -67.14) * mm});
            skLineSegment(sketch, "E511", {"start": v(183.65, -67.14) * mm, "end": v(183.8, -67.31) * mm});
            skLineSegment(sketch, "E512", {"start": v(183.8, -67.31) * mm, "end": v(188.98, -63.34) * mm});
            skLineSegment(sketch, "E513", {"start": v(188.98, -63.34) * mm, "end": v(188.85, -63.16) * mm});
            skLineSegment(sketch, "E514", {"start": v(188.85, -63.16) * mm, "end": v(186.52, -57.29) * mm});
            skLineSegment(sketch, "E515", {"start": v(186.52, -57.29) * mm, "end": v(185.35, -50.4) * mm});
            skLineSegment(sketch, "E516", {"start": v(185.35, -50.4) * mm, "end": v(189.37, -47.92) * mm});
            skLineSegment(sketch, "E517", {"start": v(189.37, -47.92) * mm, "end": v(195.02, -52.02) * mm});
            skLineSegment(sketch, "E518", {"start": v(195.02, -52.02) * mm, "end": v(199.25, -56.7) * mm});
            skLineSegment(sketch, "E519", {"start": v(199.25, -56.7) * mm, "end": v(199.35, -56.9) * mm});
            skLineSegment(sketch, "E520", {"start": v(199.35, -56.9) * mm, "end": v(205.21, -54.03) * mm});
            skLineSegment(sketch, "E521", {"start": v(205.21, -54.03) * mm, "end": v(205.12, -53.82) * mm});
            skLineSegment(sketch, "E522", {"start": v(205.12, -53.82) * mm, "end": v(203.99, -47.6) * mm});
            skLineSegment(sketch, "E523", {"start": v(203.99, -47.6) * mm, "end": v(204.18, -40.63) * mm});
            skLineSegment(sketch, "E524", {"start": v(204.18, -40.63) * mm, "end": v(208.61, -38.97) * mm});
            skLineSegment(sketch, "E525", {"start": v(208.61, -38.97) * mm, "end": v(213.35, -44.1) * mm});
            skLineSegment(sketch, "E526", {"start": v(213.35, -44.1) * mm, "end": v(216.58, -49.52) * mm});
            skLineSegment(sketch, "E527", {"start": v(216.58, -49.52) * mm, "end": v(216.65, -49.74) * mm});
            skLineSegment(sketch, "E528", {"start": v(216.65, -49.74) * mm, "end": v(222.95, -48.05) * mm});
            skLineSegment(sketch, "E529", {"start": v(222.95, -48.05) * mm, "end": v(222.9, -47.84) * mm});
            skLineSegment(sketch, "E530", {"start": v(222.9, -47.84) * mm, "end": v(223, -41.52) * mm});
            skLineSegment(sketch, "E531", {"start": v(223, -41.52) * mm, "end": v(224.56, -34.72) * mm});
            skLineSegment(sketch, "E532", {"start": v(224.56, -34.72) * mm, "end": v(229.23, -33.95) * mm});
            skLineSegment(sketch, "E533", {"start": v(229.23, -33.95) * mm, "end": v(232.87, -39.9) * mm});
            skLineSegment(sketch, "E534", {"start": v(232.87, -39.9) * mm, "end": v(234.98, -45.85) * mm});
            skLineSegment(sketch, "E535", {"start": v(234.98, -45.85) * mm, "end": v(235, -46.08) * mm});
            skLineSegment(sketch, "E536", {"start": v(235, -46.08) * mm, "end": v(241.52, -45.66) * mm});
            skLineSegment(sketch, "E537", {"start": v(241.52, -45.66) * mm, "end": v(241.51, -45.43) * mm});
            skLineSegment(sketch, "E538", {"start": v(241.51, -45.43) * mm, "end": v(242.84, -39.26) * mm});
            skLineSegment(sketch, "E539", {"start": v(242.84, -39.26) * mm, "end": v(245.7, -32.89) * mm});
            skLineSegment(sketch, "E540", {"start": v(245.7, -32.89) * mm, "end": v(250.42, -33.05) * mm});
            skLineSegment(sketch, "E541", {"start": v(250.42, -33.05) * mm, "end": v(252.83, -39.6) * mm});
            skLineSegment(sketch, "E542", {"start": v(252.83, -39.6) * mm, "end": v(253.75, -45.85) * mm});
            skLineSegment(sketch, "E543", {"start": v(253.75, -45.85) * mm, "end": v(253.73, -46.07) * mm});
            skLineSegment(sketch, "E544", {"start": v(253.73, -46.07) * mm, "end": v(260.2, -46.93) * mm});
            skLineSegment(sketch, "E545", {"start": v(260.2, -46.93) * mm, "end": v(260.23, -46.7) * mm});
            skLineSegment(sketch, "E546", {"start": v(260.23, -46.7) * mm, "end": v(262.74, -40.91) * mm});
            skLineSegment(sketch, "E547", {"start": v(262.74, -40.91) * mm, "end": v(266.78, -35.22) * mm});
            skLineSegment(sketch, "E548", {"start": v(266.78, -35.22) * mm, "end": v(271.39, -36.3) * mm});
            skLineSegment(sketch, "E549", {"start": v(271.39, -36.3) * mm, "end": v(272.48, -43.2) * mm});
            skLineSegment(sketch, "E550", {"start": v(272.48, -43.2) * mm, "end": v(272.15, -49.5) * mm});
            skLineSegment(sketch, "E551", {"start": v(272.15, -49.5) * mm, "end": v(272.09, -49.71) * mm});
            skLineSegment(sketch, "E552", {"start": v(272.09, -49.71) * mm, "end": v(278.27, -51.82) * mm});
            skLineSegment(sketch, "E553", {"start": v(278.27, -51.82) * mm, "end": v(278.34, -51.6) * mm});
            skLineSegment(sketch, "E554", {"start": v(278.34, -51.6) * mm, "end": v(281.94, -46.42) * mm});
            skLineSegment(sketch, "E555", {"start": v(281.94, -46.42) * mm, "end": v(287, -41.62) * mm});
            skLineSegment(sketch, "E556", {"start": v(287, -41.62) * mm, "end": v(291.32, -43.58) * mm});
            skLineSegment(sketch, "E557", {"start": v(291.32, -43.58) * mm, "end": v(291.04, -50.55) * mm});
            skLineSegment(sketch, "E558", {"start": v(291.04, -50.55) * mm, "end": v(289.5, -56.67) * mm});
            skLineSegment(sketch, "E559", {"start": v(289.5, -56.67) * mm, "end": v(289.38, -56.87) * mm});
            skLineSegment(sketch, "E560", {"start": v(289.38, -56.87) * mm, "end": v(295.03, -60.14) * mm});
            skLineSegment(sketch, "E561", {"start": v(295.03, -60.14) * mm, "end": v(295.15, -59.95) * mm});
            skLineSegment(sketch, "E562", {"start": v(295.15, -59.95) * mm, "end": v(299.7, -55.56) * mm});
            skLineSegment(sketch, "E563", {"start": v(299.7, -55.56) * mm, "end": v(305.6, -51.84) * mm});
            skLineSegment(sketch, "E564", {"start": v(305.6, -51.84) * mm, "end": v(309.44, -54.6) * mm});
            skLineSegment(sketch, "E565", {"start": v(309.44, -54.6) * mm, "end": v(307.8, -61.39) * mm});
            skLineSegment(sketch, "E566", {"start": v(307.8, -61.39) * mm, "end": v(305.1, -67.1) * mm});
            skLineSegment(sketch, "E567", {"start": v(305.1, -67.1) * mm, "end": v(304.95, -67.27) * mm});
            skLineSegment(sketch, "E568", {"start": v(304.95, -67.27) * mm, "end": v(309.86, -71.57) * mm});
            skLineSegment(sketch, "E569", {"start": v(309.86, -71.57) * mm, "end": v(310, -71.41) * mm});
            skLineSegment(sketch, "E570", {"start": v(310, -71.41) * mm, "end": v(315.32, -67.99) * mm});
            skLineSegment(sketch, "E571", {"start": v(315.32, -67.99) * mm, "end": v(321.84, -65.5) * mm});
            skLineSegment(sketch, "E572", {"start": v(321.84, -65.5) * mm, "end": v(325.07, -68.95) * mm});
            skLineSegment(sketch, "E573", {"start": v(325.07, -68.95) * mm, "end": v(322.14, -75.3) * mm});
            skLineSegment(sketch, "E574", {"start": v(322.14, -75.3) * mm, "end": v(318.37, -80.36) * mm});
            skLineSegment(sketch, "E575", {"start": v(318.37, -80.36) * mm, "end": v(318.2, -80.5) * mm});
            skLineSegment(sketch, "E576", {"start": v(318.2, -80.5) * mm, "end": v(322.16, -85.68) * mm});
            skLineSegment(sketch, "E577", {"start": v(322.16, -85.68) * mm, "end": v(322.35, -85.55) * mm});
            skLineSegment(sketch, "E578", {"start": v(322.35, -85.55) * mm, "end": v(328.22, -83.23) * mm});
            skLineSegment(sketch, "E579", {"start": v(328.22, -83.23) * mm, "end": v(335.1, -82.06) * mm});
            skLineSegment(sketch, "E580", {"start": v(335.1, -82.06) * mm, "end": v(337.6, -86.08) * mm});
            skLineSegment(sketch, "E581", {"start": v(337.6, -86.08) * mm, "end": v(333.49, -91.72) * mm});
            skLineSegment(sketch, "E582", {"start": v(333.49, -91.72) * mm, "end": v(328.8, -95.95) * mm});
            skLineSegment(sketch, "E583", {"start": v(328.8, -95.95) * mm, "end": v(328.6, -96.06) * mm});
            skLineSegment(sketch, "E584", {"start": v(328.6, -96.06) * mm, "end": v(331.48, -101.91) * mm});
            skLineSegment(sketch, "E585", {"start": v(331.48, -101.91) * mm, "end": v(331.69, -101.82) * mm});
            skLineSegment(sketch, "E586", {"start": v(331.69, -101.82) * mm, "end": v(337.9, -100.7) * mm});
            skLineSegment(sketch, "E587", {"start": v(337.9, -100.7) * mm, "end": v(344.88, -100.89) * mm});
            skLineSegment(sketch, "E588", {"start": v(344.88, -100.89) * mm, "end": v(346.54, -105.31) * mm});
            skLineSegment(sketch, "E589", {"start": v(346.54, -105.31) * mm, "end": v(341.41, -110.05) * mm});
            skLineSegment(sketch, "E590", {"start": v(341.41, -110.05) * mm, "end": v(335.99, -113.29) * mm});
            skLineSegment(sketch, "E591", {"start": v(335.99, -113.29) * mm, "end": v(335.77, -113.35) * mm});
            skLineSegment(sketch, "E592", {"start": v(335.77, -113.35) * mm, "end": v(337.46, -119.66) * mm});
            skLineSegment(sketch, "E593", {"start": v(337.46, -119.66) * mm, "end": v(337.67, -119.6) * mm});
            skLineSegment(sketch, "E594", {"start": v(337.67, -119.6) * mm, "end": v(343.99, -119.7) * mm});
            skLineSegment(sketch, "E595", {"start": v(343.99, -119.7) * mm, "end": v(350.8, -121.26) * mm});
            skLineSegment(sketch, "E596", {"start": v(350.8, -121.26) * mm, "end": v(351.56, -125.93) * mm});
            skLineSegment(sketch, "E597", {"start": v(351.56, -125.93) * mm, "end": v(345.6, -129.57) * mm});
            skLineSegment(sketch, "E598", {"start": v(345.6, -129.57) * mm, "end": v(339.65, -131.69) * mm});
            skLineSegment(sketch, "E599", {"start": v(339.65, -131.69) * mm, "end": v(339.43, -131.7) * mm});
            skLineSegment(sketch, "E600", {"start": v(339.43, -131.7) * mm, "end": v(339.85, -138.22) * mm});
            skLineSegment(sketch, "E601", {"start": v(0, 0) * mm, "end": v(244.4, -141.1) * mm});
            skCircle(sketch, "E602", {"center": v(244.4, -141.1) * mm, "radius": 12.5 * mm});
            skSolve(sketch);
        }
        {
            var Q0;
            Q0=makeQuery(id+"F1.imprint","IMPRINT",FACE,{"disambiguationData":[TD([[makeQuery(id+"F1.imprint","IMPRINT",EDGE,{"derivedFrom":sQuery(id+"F1.wireOp",EDGE,"E11")}),-1.0]])]});
            extrude(context, id + "F4", {"entities" : qUnion([Q0]), "depth" : 25 * mm, "offsetDistance" : 25 * mm});
        }
        {
            var Q0;
            Q0 = qSketchRegion(id + "F2", true);
            extrude(context, id + "F5", {"entities" : qUnion([Q0]), "depth" : 25 * mm, "offsetDistance" : 25 * mm});
        }
        {
            var Q0;
            {var subQ1=sQuery(id+"F0.wireOp",EDGE,"E4");var subQ3=sQuery(id+"F0.wireOp",EDGE,"E10");var subQ4=makeQuery(id+"F0.imprint","INTERSECT",VERTEX,{"derivedFrom":[subQ1,subQ3]});Q0=makeQuery(id+"F0.imprint","IMPRINT",FACE,{"disambiguationData":[TD([[makeQuery(id+"F0.imprint","IMPRINT",EDGE,{"disambiguationData":[TD([[subQ4,1.0]])],"derivedFrom":subQ3}),1.0]])]});}
            var Q1;
            {var subQ1=sQuery(id+"F0.wireOp",EDGE,"E5");var subQ3=sQuery(id+"F0.wireOp",EDGE,"E10");var subQ4=makeQuery(id+"F0.imprint","INTERSECT",VERTEX,{"derivedFrom":[subQ1,subQ3]});Q1=makeQuery(id+"F0.imprint","IMPRINT",FACE,{"disambiguationData":[TD([[makeQuery(id+"F0.imprint","IMPRINT",EDGE,{"disambiguationData":[TD([[subQ4,1.0]])],"derivedFrom":subQ3}),1.0]])]});}
            var Q2;
            {var subQ1=sQuery(id+"F0.wireOp",EDGE,"E4");var subQ3=sQuery(id+"F0.wireOp",EDGE,"E10");var subQ4=makeQuery(id+"F0.imprint","INTERSECT",VERTEX,{"derivedFrom":[subQ1,subQ3]});Q2=makeQuery(id+"F0.imprint","IMPRINT",FACE,{"disambiguationData":[TD([[makeQuery(id+"F0.imprint","IMPRINT",EDGE,{"disambiguationData":[TD([[subQ4,-1.0]])],"derivedFrom":subQ3}),1.0]])]});}
            var Q3;
            Q3=makeQuery(id+"F0.imprint","IMPRINT",FACE,{"disambiguationData":[TD([[makeQuery(id+"F0.imprint","IMPRINT",EDGE,{"derivedFrom":sQuery(id+"F0.wireOp",EDGE,"E8")}),1.0]])]});
            var Q4;
            Q4=makeQuery(id+"F0.imprint","IMPRINT",FACE,{"disambiguationData":[TD([[makeQuery(id+"F0.imprint","IMPRINT",EDGE,{"derivedFrom":sQuery(id+"F0.wireOp",EDGE,"E9")}),1.0]])]});
            var Q5;
            Q5=makeQuery(id+"F0.imprint","IMPRINT",FACE,{"disambiguationData":[TD([[makeQuery(id+"F0.imprint","IMPRINT",EDGE,{"derivedFrom":sQuery(id+"F0.wireOp",EDGE,"E7")}),1.0]])]});
            extrude(context, id + "F6", {"entities" : qUnion([Q0, Q1, Q2, Q3, Q4, Q5]), "depth" : 35 * mm, "offsetDistance" : 25 * mm});
        }
        {
            var Q0;
            Q0 = qSketchRegion(id + "F3", true);
            extrude(context, id + "F7", {"entities" : qUnion([Q0]), "depth" : 25 * mm, "offsetDistance" : 25 * mm});
        }
    });
